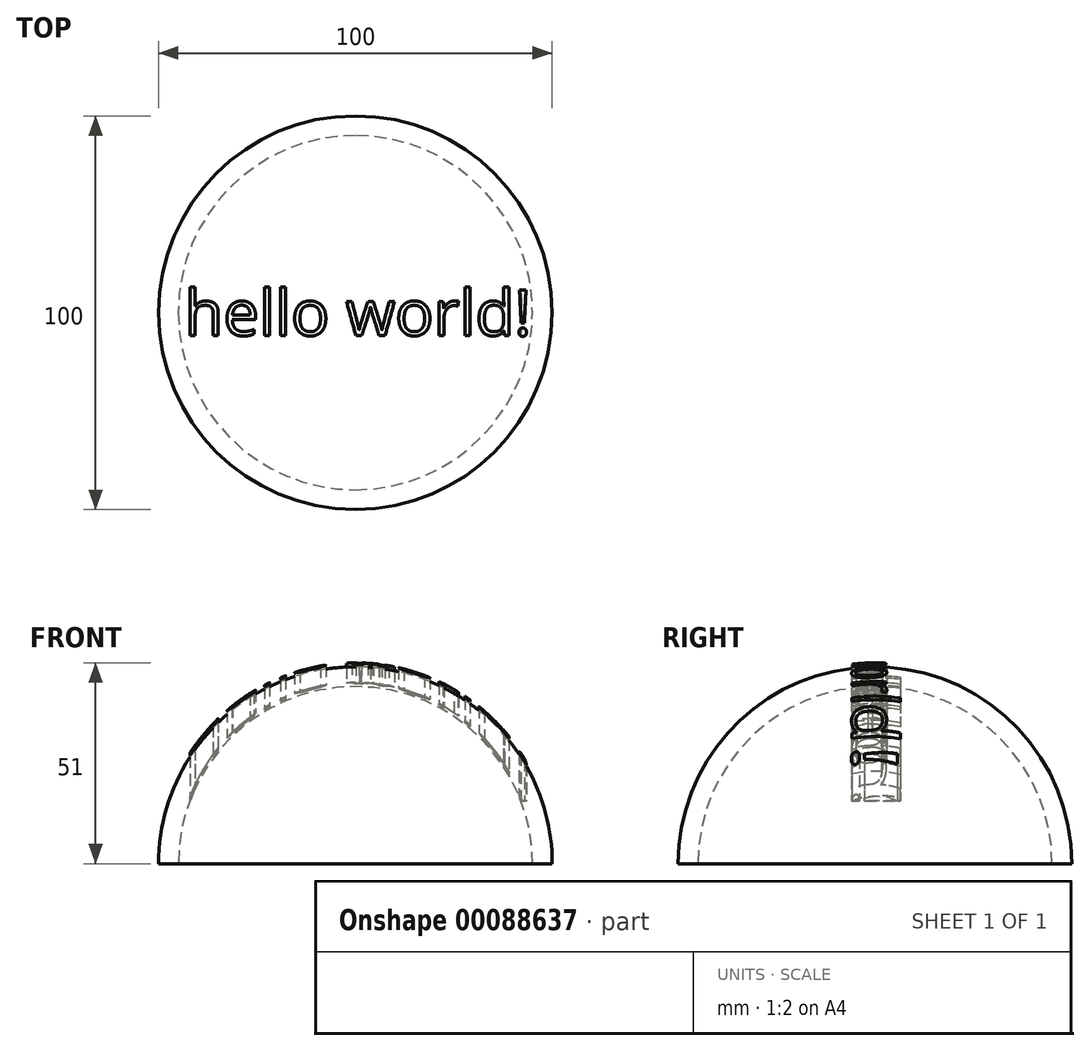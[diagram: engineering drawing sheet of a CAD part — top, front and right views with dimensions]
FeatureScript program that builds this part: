
annotation { "Feature Type Name" : "Feature", "Feature Type Description" : "" }
export const myFeature = defineFeature(function(context is Context, id is Id, definition is map)
    precondition{}
    {
        {
            var Q0;
            Q0=qCreatedBy(makeId("Top.planeOp"),FACE);
            var sketch = newSketch(context, id + "F0", { "sketchPlane" : qUnion([Q0])});
            skPoint(sketch, "E0", {"position": v(0, 50) * mm});
            skPoint(sketch, "E1", {"position": v(0, -50) * mm});
            skArc(sketch, "E2", {"start": v(0, 50) * mm, "mid": v(-50, 0) * mm, "end": v(0, -50) * mm});
            skPoint(sketch, "E3", {"position": v(0, 45) * mm});
            skPoint(sketch, "E4", {"position": v(0, -45) * mm});
            skArc(sketch, "E5", {"start": v(0, 45) * mm, "mid": v(-45, 0) * mm, "end": v(0, -45) * mm});
            skLineSegment(sketch, "E6", {"start": v(0, 45) * mm, "end": v(0, 50) * mm});
            skLineSegment(sketch, "E7", {"start": v(0, -45) * mm, "end": v(0, -50) * mm});
            skSolve(sketch);
        }
        {
            var Q0;
            Q0=makeQuery(id+"F0.imprint","IMPRINT",FACE,{"disambiguationData":[TD([[makeQuery(id+"F0.imprint","IMPRINT",EDGE,{"derivedFrom":sQuery(id+"F0.wireOp",EDGE,"E2")}),1.0]])]});
            var Q1;
            Q1=sQuery(id+"F0.wireOp",EDGE,"E6");
            revolve(context, id + "F1", {"entities" : qUnion([Q0]), "axis" : qUnion([Q1]), "revolveType" : RevolveType.ONE_DIRECTION, "angle" : 180 * degree});
        }
        {
            var Q0;
            Q0=makeQuery(id+"F1.opRevolve","SWEPT_BODY",BODY,{"disambiguationData":[OSD([sQuery(id+"F0.wireOp",EDGE,"E2"),sQuery(id+"F0.wireOp",EDGE,"E5"),sQuery(id+"F0.wireOp",EDGE,"E6"),sQuery(id+"F0.wireOp",EDGE,"E7")])]});
            transform(context, id + "F2", {"entities" : qUnion([Q0]), "transformType" : TransformType.TRANSLATION_3D, "dx" : 0 * mm, "dy" : 0 * mm, "dz" : 0 * mm, "makeCopy" : true});
        }
        {
            var Q0;
            Q0=qCreatedBy(makeId("Top.planeOp"),FACE);
            var sketch = newSketch(context, id + "F3", { "sketchPlane" : qUnion([Q0])});
            skText(sketch, "E8", { "text": "hello world!", "fontName": "OpenSans-Regular.ttf"});
            skLineSegment(sketch, "E9", {"start": v(-43.42, 5.8) * mm, "end": v(43.42, -5.8) * mm, "construction": true});
            skLineSegment(sketch, "E10", {"start": v(-43.42, -5.8) * mm, "end": v(43.42, 5.8) * mm, "construction": true});
            skPoint(sketch, "E11", {"position": v(0, 0) * mm});
            const initialGuessF3  = {"E8": [-0.04342, -0.0058, 1, 0, 0.0116]};
            skSetInitialGuess(sketch, initialGuessF3);
            skSolve(sketch);
        }
        {
            var Q0;
            Q0 = qSketchRegion(id + "F3", true);
            extrude(context, id + "F4", {"entities" : qUnion([Q0]), "endBound" : BoundingType.UP_TO_NEXT, "depth" : 100 * mm});
        }
        {
            var Q0;
            Q0=makeQuery(id+"F4.opExtrude","SWEPT_BODY",BODY,{"disambiguationData":[OSD([sQuery(id+"F3.wireOp",EDGE,"E8.sketch_text.stroke-0"),sQuery(id+"F3.wireOp",EDGE,"E8.sketch_text.stroke-1"),sQuery(id+"F3.wireOp",EDGE,"E8.sketch_text.stroke-2"),sQuery(id+"F3.wireOp",EDGE,"E8.sketch_text.stroke-3"),sQuery(id+"F3.wireOp",EDGE,"E8.sketch_text.stroke-4"),sQuery(id+"F3.wireOp",EDGE,"E8.sketch_text.stroke-5"),sQuery(id+"F3.wireOp",EDGE,"E8.sketch_text.stroke-6"),sQuery(id+"F3.wireOp",EDGE,"E8.sketch_text.stroke-7"),sQuery(id+"F3.wireOp",EDGE,"E8.sketch_text.stroke-8"),sQuery(id+"F3.wireOp",EDGE,"E8.sketch_text.stroke-9"),sQuery(id+"F3.wireOp",EDGE,"E8.sketch_text.stroke-10"),sQuery(id+"F3.wireOp",EDGE,"E8.sketch_text.stroke-11"),sQuery(id+"F3.wireOp",EDGE,"E8.sketch_text.stroke-12"),sQuery(id+"F3.wireOp",EDGE,"E8.sketch_text.stroke-13"),sQuery(id+"F3.wireOp",EDGE,"E8.sketch_text.stroke-14"),sQuery(id+"F3.wireOp",EDGE,"E8.sketch_text.stroke-15"),sQuery(id+"F3.wireOp",EDGE,"E8.sketch_text.stroke-16"),sQuery(id+"F3.wireOp",EDGE,"E8.sketch_text.stroke-17")])]});
            var Q1;
            Q1=makeQuery(id+"F4.opExtrude","SWEPT_BODY",BODY,{"disambiguationData":[OSD([sQuery(id+"F3.wireOp",EDGE,"E8.sketch_text.stroke-18"),sQuery(id+"F3.wireOp",EDGE,"E8.sketch_text.stroke-19"),sQuery(id+"F3.wireOp",EDGE,"E8.sketch_text.stroke-20"),sQuery(id+"F3.wireOp",EDGE,"E8.sketch_text.stroke-21"),sQuery(id+"F3.wireOp",EDGE,"E8.sketch_text.stroke-22"),sQuery(id+"F3.wireOp",EDGE,"E8.sketch_text.stroke-23"),sQuery(id+"F3.wireOp",EDGE,"E8.sketch_text.stroke-24"),sQuery(id+"F3.wireOp",EDGE,"E8.sketch_text.stroke-25"),sQuery(id+"F3.wireOp",EDGE,"E8.sketch_text.stroke-26"),sQuery(id+"F3.wireOp",EDGE,"E8.sketch_text.stroke-27"),sQuery(id+"F3.wireOp",EDGE,"E8.sketch_text.stroke-28"),sQuery(id+"F3.wireOp",EDGE,"E8.sketch_text.stroke-29"),sQuery(id+"F3.wireOp",EDGE,"E8.sketch_text.stroke-30"),sQuery(id+"F3.wireOp",EDGE,"E8.sketch_text.stroke-31"),sQuery(id+"F3.wireOp",EDGE,"E8.sketch_text.stroke-32"),sQuery(id+"F3.wireOp",EDGE,"E8.sketch_text.stroke-33"),sQuery(id+"F3.wireOp",EDGE,"E8.sketch_text.stroke-34"),sQuery(id+"F3.wireOp",EDGE,"E8.sketch_text.stroke-35"),sQuery(id+"F3.wireOp",EDGE,"E8.sketch_text.stroke-36")])]});
            var Q2;
            Q2=makeQuery(id+"F4.opExtrude","SWEPT_BODY",BODY,{"disambiguationData":[OSD([sQuery(id+"F3.wireOp",EDGE,"E8.sketch_text.stroke-37"),sQuery(id+"F3.wireOp",EDGE,"E8.sketch_text.stroke-38"),sQuery(id+"F3.wireOp",EDGE,"E8.sketch_text.stroke-39"),sQuery(id+"F3.wireOp",EDGE,"E8.sketch_text.stroke-40")])]});
            var Q3;
            Q3=makeQuery(id+"F4.opExtrude","SWEPT_BODY",BODY,{"disambiguationData":[OSD([sQuery(id+"F3.wireOp",EDGE,"E8.sketch_text.stroke-41"),sQuery(id+"F3.wireOp",EDGE,"E8.sketch_text.stroke-42"),sQuery(id+"F3.wireOp",EDGE,"E8.sketch_text.stroke-43"),sQuery(id+"F3.wireOp",EDGE,"E8.sketch_text.stroke-44")])]});
            var Q4;
            Q4=makeQuery(id+"F4.opExtrude","SWEPT_BODY",BODY,{"disambiguationData":[OSD([sQuery(id+"F3.wireOp",EDGE,"E8.sketch_text.stroke-45"),sQuery(id+"F3.wireOp",EDGE,"E8.sketch_text.stroke-46"),sQuery(id+"F3.wireOp",EDGE,"E8.sketch_text.stroke-47"),sQuery(id+"F3.wireOp",EDGE,"E8.sketch_text.stroke-48"),sQuery(id+"F3.wireOp",EDGE,"E8.sketch_text.stroke-49"),sQuery(id+"F3.wireOp",EDGE,"E8.sketch_text.stroke-50"),sQuery(id+"F3.wireOp",EDGE,"E8.sketch_text.stroke-51"),sQuery(id+"F3.wireOp",EDGE,"E8.sketch_text.stroke-52"),sQuery(id+"F3.wireOp",EDGE,"E8.sketch_text.stroke-53"),sQuery(id+"F3.wireOp",EDGE,"E8.sketch_text.stroke-54"),sQuery(id+"F3.wireOp",EDGE,"E8.sketch_text.stroke-55"),sQuery(id+"F3.wireOp",EDGE,"E8.sketch_text.stroke-56"),sQuery(id+"F3.wireOp",EDGE,"E8.sketch_text.stroke-57"),sQuery(id+"F3.wireOp",EDGE,"E8.sketch_text.stroke-58"),sQuery(id+"F3.wireOp",EDGE,"E8.sketch_text.stroke-59"),sQuery(id+"F3.wireOp",EDGE,"E8.sketch_text.stroke-60"),sQuery(id+"F3.wireOp",EDGE,"E8.sketch_text.stroke-61")])]});
            var Q5;
            Q5=makeQuery(id+"F4.opExtrude","SWEPT_BODY",BODY,{"disambiguationData":[OSD([sQuery(id+"F3.wireOp",EDGE,"E8.sketch_text.stroke-62"),sQuery(id+"F3.wireOp",EDGE,"E8.sketch_text.stroke-63"),sQuery(id+"F3.wireOp",EDGE,"E8.sketch_text.stroke-64"),sQuery(id+"F3.wireOp",EDGE,"E8.sketch_text.stroke-65"),sQuery(id+"F3.wireOp",EDGE,"E8.sketch_text.stroke-66"),sQuery(id+"F3.wireOp",EDGE,"E8.sketch_text.stroke-67"),sQuery(id+"F3.wireOp",EDGE,"E8.sketch_text.stroke-68"),sQuery(id+"F3.wireOp",EDGE,"E8.sketch_text.stroke-69"),sQuery(id+"F3.wireOp",EDGE,"E8.sketch_text.stroke-70"),sQuery(id+"F3.wireOp",EDGE,"E8.sketch_text.stroke-71"),sQuery(id+"F3.wireOp",EDGE,"E8.sketch_text.stroke-72"),sQuery(id+"F3.wireOp",EDGE,"E8.sketch_text.stroke-73"),sQuery(id+"F3.wireOp",EDGE,"E8.sketch_text.stroke-74"),sQuery(id+"F3.wireOp",EDGE,"E8.sketch_text.stroke-75"),sQuery(id+"F3.wireOp",EDGE,"E8.sketch_text.stroke-76"),sQuery(id+"F3.wireOp",EDGE,"E8.sketch_text.stroke-77"),sQuery(id+"F3.wireOp",EDGE,"E8.sketch_text.stroke-78"),sQuery(id+"F3.wireOp",EDGE,"E8.sketch_text.stroke-79"),sQuery(id+"F3.wireOp",EDGE,"E8.sketch_text.stroke-80"),sQuery(id+"F3.wireOp",EDGE,"E8.sketch_text.stroke-81"),sQuery(id+"F3.wireOp",EDGE,"E8.sketch_text.stroke-82"),sQuery(id+"F3.wireOp",EDGE,"E8.sketch_text.stroke-83"),sQuery(id+"F3.wireOp",EDGE,"E8.sketch_text.stroke-84")])]});
            var Q6;
            Q6=makeQuery(id+"F4.opExtrude","SWEPT_BODY",BODY,{"disambiguationData":[OSD([sQuery(id+"F3.wireOp",EDGE,"E8.sketch_text.stroke-85"),sQuery(id+"F3.wireOp",EDGE,"E8.sketch_text.stroke-86"),sQuery(id+"F3.wireOp",EDGE,"E8.sketch_text.stroke-87"),sQuery(id+"F3.wireOp",EDGE,"E8.sketch_text.stroke-88"),sQuery(id+"F3.wireOp",EDGE,"E8.sketch_text.stroke-89"),sQuery(id+"F3.wireOp",EDGE,"E8.sketch_text.stroke-90"),sQuery(id+"F3.wireOp",EDGE,"E8.sketch_text.stroke-91"),sQuery(id+"F3.wireOp",EDGE,"E8.sketch_text.stroke-92"),sQuery(id+"F3.wireOp",EDGE,"E8.sketch_text.stroke-93"),sQuery(id+"F3.wireOp",EDGE,"E8.sketch_text.stroke-94"),sQuery(id+"F3.wireOp",EDGE,"E8.sketch_text.stroke-95"),sQuery(id+"F3.wireOp",EDGE,"E8.sketch_text.stroke-96"),sQuery(id+"F3.wireOp",EDGE,"E8.sketch_text.stroke-97"),sQuery(id+"F3.wireOp",EDGE,"E8.sketch_text.stroke-98"),sQuery(id+"F3.wireOp",EDGE,"E8.sketch_text.stroke-99"),sQuery(id+"F3.wireOp",EDGE,"E8.sketch_text.stroke-100"),sQuery(id+"F3.wireOp",EDGE,"E8.sketch_text.stroke-101")])]});
            var Q7;
            Q7=makeQuery(id+"F4.opExtrude","SWEPT_BODY",BODY,{"disambiguationData":[OSD([sQuery(id+"F3.wireOp",EDGE,"E8.sketch_text.stroke-102"),sQuery(id+"F3.wireOp",EDGE,"E8.sketch_text.stroke-103"),sQuery(id+"F3.wireOp",EDGE,"E8.sketch_text.stroke-104"),sQuery(id+"F3.wireOp",EDGE,"E8.sketch_text.stroke-105"),sQuery(id+"F3.wireOp",EDGE,"E8.sketch_text.stroke-106"),sQuery(id+"F3.wireOp",EDGE,"E8.sketch_text.stroke-107"),sQuery(id+"F3.wireOp",EDGE,"E8.sketch_text.stroke-108"),sQuery(id+"F3.wireOp",EDGE,"E8.sketch_text.stroke-109"),sQuery(id+"F3.wireOp",EDGE,"E8.sketch_text.stroke-110"),sQuery(id+"F3.wireOp",EDGE,"E8.sketch_text.stroke-111"),sQuery(id+"F3.wireOp",EDGE,"E8.sketch_text.stroke-112"),sQuery(id+"F3.wireOp",EDGE,"E8.sketch_text.stroke-113"),sQuery(id+"F3.wireOp",EDGE,"E8.sketch_text.stroke-114")])]});
            var Q8;
            Q8=makeQuery(id+"F4.opExtrude","SWEPT_BODY",BODY,{"disambiguationData":[OSD([sQuery(id+"F3.wireOp",EDGE,"E8.sketch_text.stroke-115"),sQuery(id+"F3.wireOp",EDGE,"E8.sketch_text.stroke-116"),sQuery(id+"F3.wireOp",EDGE,"E8.sketch_text.stroke-117"),sQuery(id+"F3.wireOp",EDGE,"E8.sketch_text.stroke-118")])]});
            var Q9;
            Q9=makeQuery(id+"F4.opExtrude","SWEPT_BODY",BODY,{"disambiguationData":[OSD([sQuery(id+"F3.wireOp",EDGE,"E8.sketch_text.stroke-119"),sQuery(id+"F3.wireOp",EDGE,"E8.sketch_text.stroke-120"),sQuery(id+"F3.wireOp",EDGE,"E8.sketch_text.stroke-121"),sQuery(id+"F3.wireOp",EDGE,"E8.sketch_text.stroke-122"),sQuery(id+"F3.wireOp",EDGE,"E8.sketch_text.stroke-123"),sQuery(id+"F3.wireOp",EDGE,"E8.sketch_text.stroke-124"),sQuery(id+"F3.wireOp",EDGE,"E8.sketch_text.stroke-125"),sQuery(id+"F3.wireOp",EDGE,"E8.sketch_text.stroke-126"),sQuery(id+"F3.wireOp",EDGE,"E8.sketch_text.stroke-127"),sQuery(id+"F3.wireOp",EDGE,"E8.sketch_text.stroke-128"),sQuery(id+"F3.wireOp",EDGE,"E8.sketch_text.stroke-129"),sQuery(id+"F3.wireOp",EDGE,"E8.sketch_text.stroke-130"),sQuery(id+"F3.wireOp",EDGE,"E8.sketch_text.stroke-131"),sQuery(id+"F3.wireOp",EDGE,"E8.sketch_text.stroke-132"),sQuery(id+"F3.wireOp",EDGE,"E8.sketch_text.stroke-133"),sQuery(id+"F3.wireOp",EDGE,"E8.sketch_text.stroke-134"),sQuery(id+"F3.wireOp",EDGE,"E8.sketch_text.stroke-135"),sQuery(id+"F3.wireOp",EDGE,"E8.sketch_text.stroke-136"),sQuery(id+"F3.wireOp",EDGE,"E8.sketch_text.stroke-137"),sQuery(id+"F3.wireOp",EDGE,"E8.sketch_text.stroke-138"),sQuery(id+"F3.wireOp",EDGE,"E8.sketch_text.stroke-139"),sQuery(id+"F3.wireOp",EDGE,"E8.sketch_text.stroke-140"),sQuery(id+"F3.wireOp",EDGE,"E8.sketch_text.stroke-141"),sQuery(id+"F3.wireOp",EDGE,"E8.sketch_text.stroke-142")])]});
            var Q10;
            Q10=makeQuery(id+"F4.opExtrude","SWEPT_BODY",BODY,{"disambiguationData":[OSD([sQuery(id+"F3.wireOp",EDGE,"E8.sketch_text.stroke-143"),sQuery(id+"F3.wireOp",EDGE,"E8.sketch_text.stroke-144"),sQuery(id+"F3.wireOp",EDGE,"E8.sketch_text.stroke-145"),sQuery(id+"F3.wireOp",EDGE,"E8.sketch_text.stroke-146")])]});
            var Q11;
            Q11=makeQuery(id+"F4.opExtrude","SWEPT_BODY",BODY,{"disambiguationData":[OSD([sQuery(id+"F3.wireOp",EDGE,"E8.sketch_text.stroke-147"),sQuery(id+"F3.wireOp",EDGE,"E8.sketch_text.stroke-148"),sQuery(id+"F3.wireOp",EDGE,"E8.sketch_text.stroke-149"),sQuery(id+"F3.wireOp",EDGE,"E8.sketch_text.stroke-150"),sQuery(id+"F3.wireOp",EDGE,"E8.sketch_text.stroke-151"),sQuery(id+"F3.wireOp",EDGE,"E8.sketch_text.stroke-152"),sQuery(id+"F3.wireOp",EDGE,"E8.sketch_text.stroke-153")])]});
            transform(context, id + "F5", {"entities" : qUnion([Q0, Q1, Q2, Q3, Q4, Q5, Q6, Q7, Q8, Q9, Q10, Q11]), "transformType" : TransformType.TRANSLATION_3D, "dx" : 0 * mm, "dy" : 0 * mm, "dz" : 10 * mm, "makeCopy" : false});
        }
        {
            var Q0;
            Q0=makeQuery(id+"F4.opExtrude","SWEPT_BODY",BODY,{"disambiguationData":[OSD([sQuery(id+"F3.wireOp",EDGE,"E8.sketch_text.stroke-0"),sQuery(id+"F3.wireOp",EDGE,"E8.sketch_text.stroke-1"),sQuery(id+"F3.wireOp",EDGE,"E8.sketch_text.stroke-2"),sQuery(id+"F3.wireOp",EDGE,"E8.sketch_text.stroke-3"),sQuery(id+"F3.wireOp",EDGE,"E8.sketch_text.stroke-4"),sQuery(id+"F3.wireOp",EDGE,"E8.sketch_text.stroke-5"),sQuery(id+"F3.wireOp",EDGE,"E8.sketch_text.stroke-6"),sQuery(id+"F3.wireOp",EDGE,"E8.sketch_text.stroke-7"),sQuery(id+"F3.wireOp",EDGE,"E8.sketch_text.stroke-8"),sQuery(id+"F3.wireOp",EDGE,"E8.sketch_text.stroke-9"),sQuery(id+"F3.wireOp",EDGE,"E8.sketch_text.stroke-10"),sQuery(id+"F3.wireOp",EDGE,"E8.sketch_text.stroke-11"),sQuery(id+"F3.wireOp",EDGE,"E8.sketch_text.stroke-12"),sQuery(id+"F3.wireOp",EDGE,"E8.sketch_text.stroke-13"),sQuery(id+"F3.wireOp",EDGE,"E8.sketch_text.stroke-14"),sQuery(id+"F3.wireOp",EDGE,"E8.sketch_text.stroke-15"),sQuery(id+"F3.wireOp",EDGE,"E8.sketch_text.stroke-16"),sQuery(id+"F3.wireOp",EDGE,"E8.sketch_text.stroke-17")])]});
            var Q1;
            Q1=makeQuery(id+"F4.opExtrude","SWEPT_BODY",BODY,{"disambiguationData":[OSD([sQuery(id+"F3.wireOp",EDGE,"E8.sketch_text.stroke-18"),sQuery(id+"F3.wireOp",EDGE,"E8.sketch_text.stroke-19"),sQuery(id+"F3.wireOp",EDGE,"E8.sketch_text.stroke-20"),sQuery(id+"F3.wireOp",EDGE,"E8.sketch_text.stroke-21"),sQuery(id+"F3.wireOp",EDGE,"E8.sketch_text.stroke-22"),sQuery(id+"F3.wireOp",EDGE,"E8.sketch_text.stroke-23"),sQuery(id+"F3.wireOp",EDGE,"E8.sketch_text.stroke-24"),sQuery(id+"F3.wireOp",EDGE,"E8.sketch_text.stroke-25"),sQuery(id+"F3.wireOp",EDGE,"E8.sketch_text.stroke-26"),sQuery(id+"F3.wireOp",EDGE,"E8.sketch_text.stroke-27"),sQuery(id+"F3.wireOp",EDGE,"E8.sketch_text.stroke-28"),sQuery(id+"F3.wireOp",EDGE,"E8.sketch_text.stroke-29"),sQuery(id+"F3.wireOp",EDGE,"E8.sketch_text.stroke-30"),sQuery(id+"F3.wireOp",EDGE,"E8.sketch_text.stroke-31"),sQuery(id+"F3.wireOp",EDGE,"E8.sketch_text.stroke-32"),sQuery(id+"F3.wireOp",EDGE,"E8.sketch_text.stroke-33"),sQuery(id+"F3.wireOp",EDGE,"E8.sketch_text.stroke-34"),sQuery(id+"F3.wireOp",EDGE,"E8.sketch_text.stroke-35"),sQuery(id+"F3.wireOp",EDGE,"E8.sketch_text.stroke-36")])]});
            var Q2;
            Q2=makeQuery(id+"F4.opExtrude","SWEPT_BODY",BODY,{"disambiguationData":[OSD([sQuery(id+"F3.wireOp",EDGE,"E8.sketch_text.stroke-37"),sQuery(id+"F3.wireOp",EDGE,"E8.sketch_text.stroke-38"),sQuery(id+"F3.wireOp",EDGE,"E8.sketch_text.stroke-39"),sQuery(id+"F3.wireOp",EDGE,"E8.sketch_text.stroke-40")])]});
            var Q3;
            Q3=makeQuery(id+"F4.opExtrude","SWEPT_BODY",BODY,{"disambiguationData":[OSD([sQuery(id+"F3.wireOp",EDGE,"E8.sketch_text.stroke-41"),sQuery(id+"F3.wireOp",EDGE,"E8.sketch_text.stroke-42"),sQuery(id+"F3.wireOp",EDGE,"E8.sketch_text.stroke-43"),sQuery(id+"F3.wireOp",EDGE,"E8.sketch_text.stroke-44")])]});
            var Q4;
            Q4=makeQuery(id+"F4.opExtrude","SWEPT_BODY",BODY,{"disambiguationData":[OSD([sQuery(id+"F3.wireOp",EDGE,"E8.sketch_text.stroke-45"),sQuery(id+"F3.wireOp",EDGE,"E8.sketch_text.stroke-46"),sQuery(id+"F3.wireOp",EDGE,"E8.sketch_text.stroke-47"),sQuery(id+"F3.wireOp",EDGE,"E8.sketch_text.stroke-48"),sQuery(id+"F3.wireOp",EDGE,"E8.sketch_text.stroke-49"),sQuery(id+"F3.wireOp",EDGE,"E8.sketch_text.stroke-50"),sQuery(id+"F3.wireOp",EDGE,"E8.sketch_text.stroke-51"),sQuery(id+"F3.wireOp",EDGE,"E8.sketch_text.stroke-52"),sQuery(id+"F3.wireOp",EDGE,"E8.sketch_text.stroke-53"),sQuery(id+"F3.wireOp",EDGE,"E8.sketch_text.stroke-54"),sQuery(id+"F3.wireOp",EDGE,"E8.sketch_text.stroke-55"),sQuery(id+"F3.wireOp",EDGE,"E8.sketch_text.stroke-56"),sQuery(id+"F3.wireOp",EDGE,"E8.sketch_text.stroke-57"),sQuery(id+"F3.wireOp",EDGE,"E8.sketch_text.stroke-58"),sQuery(id+"F3.wireOp",EDGE,"E8.sketch_text.stroke-59"),sQuery(id+"F3.wireOp",EDGE,"E8.sketch_text.stroke-60"),sQuery(id+"F3.wireOp",EDGE,"E8.sketch_text.stroke-61")])]});
            var Q5;
            Q5=makeQuery(id+"F4.opExtrude","SWEPT_BODY",BODY,{"disambiguationData":[OSD([sQuery(id+"F3.wireOp",EDGE,"E8.sketch_text.stroke-62"),sQuery(id+"F3.wireOp",EDGE,"E8.sketch_text.stroke-63"),sQuery(id+"F3.wireOp",EDGE,"E8.sketch_text.stroke-64"),sQuery(id+"F3.wireOp",EDGE,"E8.sketch_text.stroke-65"),sQuery(id+"F3.wireOp",EDGE,"E8.sketch_text.stroke-66"),sQuery(id+"F3.wireOp",EDGE,"E8.sketch_text.stroke-67"),sQuery(id+"F3.wireOp",EDGE,"E8.sketch_text.stroke-68"),sQuery(id+"F3.wireOp",EDGE,"E8.sketch_text.stroke-69"),sQuery(id+"F3.wireOp",EDGE,"E8.sketch_text.stroke-70"),sQuery(id+"F3.wireOp",EDGE,"E8.sketch_text.stroke-71"),sQuery(id+"F3.wireOp",EDGE,"E8.sketch_text.stroke-72"),sQuery(id+"F3.wireOp",EDGE,"E8.sketch_text.stroke-73"),sQuery(id+"F3.wireOp",EDGE,"E8.sketch_text.stroke-74"),sQuery(id+"F3.wireOp",EDGE,"E8.sketch_text.stroke-75"),sQuery(id+"F3.wireOp",EDGE,"E8.sketch_text.stroke-76"),sQuery(id+"F3.wireOp",EDGE,"E8.sketch_text.stroke-77"),sQuery(id+"F3.wireOp",EDGE,"E8.sketch_text.stroke-78"),sQuery(id+"F3.wireOp",EDGE,"E8.sketch_text.stroke-79"),sQuery(id+"F3.wireOp",EDGE,"E8.sketch_text.stroke-80"),sQuery(id+"F3.wireOp",EDGE,"E8.sketch_text.stroke-81"),sQuery(id+"F3.wireOp",EDGE,"E8.sketch_text.stroke-82"),sQuery(id+"F3.wireOp",EDGE,"E8.sketch_text.stroke-83"),sQuery(id+"F3.wireOp",EDGE,"E8.sketch_text.stroke-84")])]});
            var Q6;
            Q6=makeQuery(id+"F4.opExtrude","SWEPT_BODY",BODY,{"disambiguationData":[OSD([sQuery(id+"F3.wireOp",EDGE,"E8.sketch_text.stroke-85"),sQuery(id+"F3.wireOp",EDGE,"E8.sketch_text.stroke-86"),sQuery(id+"F3.wireOp",EDGE,"E8.sketch_text.stroke-87"),sQuery(id+"F3.wireOp",EDGE,"E8.sketch_text.stroke-88"),sQuery(id+"F3.wireOp",EDGE,"E8.sketch_text.stroke-89"),sQuery(id+"F3.wireOp",EDGE,"E8.sketch_text.stroke-90"),sQuery(id+"F3.wireOp",EDGE,"E8.sketch_text.stroke-91"),sQuery(id+"F3.wireOp",EDGE,"E8.sketch_text.stroke-92"),sQuery(id+"F3.wireOp",EDGE,"E8.sketch_text.stroke-93"),sQuery(id+"F3.wireOp",EDGE,"E8.sketch_text.stroke-94"),sQuery(id+"F3.wireOp",EDGE,"E8.sketch_text.stroke-95"),sQuery(id+"F3.wireOp",EDGE,"E8.sketch_text.stroke-96"),sQuery(id+"F3.wireOp",EDGE,"E8.sketch_text.stroke-97"),sQuery(id+"F3.wireOp",EDGE,"E8.sketch_text.stroke-98"),sQuery(id+"F3.wireOp",EDGE,"E8.sketch_text.stroke-99"),sQuery(id+"F3.wireOp",EDGE,"E8.sketch_text.stroke-100"),sQuery(id+"F3.wireOp",EDGE,"E8.sketch_text.stroke-101")])]});
            var Q7;
            Q7=makeQuery(id+"F4.opExtrude","SWEPT_BODY",BODY,{"disambiguationData":[OSD([sQuery(id+"F3.wireOp",EDGE,"E8.sketch_text.stroke-102"),sQuery(id+"F3.wireOp",EDGE,"E8.sketch_text.stroke-103"),sQuery(id+"F3.wireOp",EDGE,"E8.sketch_text.stroke-104"),sQuery(id+"F3.wireOp",EDGE,"E8.sketch_text.stroke-105"),sQuery(id+"F3.wireOp",EDGE,"E8.sketch_text.stroke-106"),sQuery(id+"F3.wireOp",EDGE,"E8.sketch_text.stroke-107"),sQuery(id+"F3.wireOp",EDGE,"E8.sketch_text.stroke-108"),sQuery(id+"F3.wireOp",EDGE,"E8.sketch_text.stroke-109"),sQuery(id+"F3.wireOp",EDGE,"E8.sketch_text.stroke-110"),sQuery(id+"F3.wireOp",EDGE,"E8.sketch_text.stroke-111"),sQuery(id+"F3.wireOp",EDGE,"E8.sketch_text.stroke-112"),sQuery(id+"F3.wireOp",EDGE,"E8.sketch_text.stroke-113"),sQuery(id+"F3.wireOp",EDGE,"E8.sketch_text.stroke-114")])]});
            var Q8;
            Q8=makeQuery(id+"F4.opExtrude","SWEPT_BODY",BODY,{"disambiguationData":[OSD([sQuery(id+"F3.wireOp",EDGE,"E8.sketch_text.stroke-115"),sQuery(id+"F3.wireOp",EDGE,"E8.sketch_text.stroke-116"),sQuery(id+"F3.wireOp",EDGE,"E8.sketch_text.stroke-117"),sQuery(id+"F3.wireOp",EDGE,"E8.sketch_text.stroke-118")])]});
            var Q9;
            Q9=makeQuery(id+"F4.opExtrude","SWEPT_BODY",BODY,{"disambiguationData":[OSD([sQuery(id+"F3.wireOp",EDGE,"E8.sketch_text.stroke-119"),sQuery(id+"F3.wireOp",EDGE,"E8.sketch_text.stroke-120"),sQuery(id+"F3.wireOp",EDGE,"E8.sketch_text.stroke-121"),sQuery(id+"F3.wireOp",EDGE,"E8.sketch_text.stroke-122"),sQuery(id+"F3.wireOp",EDGE,"E8.sketch_text.stroke-123"),sQuery(id+"F3.wireOp",EDGE,"E8.sketch_text.stroke-124"),sQuery(id+"F3.wireOp",EDGE,"E8.sketch_text.stroke-125"),sQuery(id+"F3.wireOp",EDGE,"E8.sketch_text.stroke-126"),sQuery(id+"F3.wireOp",EDGE,"E8.sketch_text.stroke-127"),sQuery(id+"F3.wireOp",EDGE,"E8.sketch_text.stroke-128"),sQuery(id+"F3.wireOp",EDGE,"E8.sketch_text.stroke-129"),sQuery(id+"F3.wireOp",EDGE,"E8.sketch_text.stroke-130"),sQuery(id+"F3.wireOp",EDGE,"E8.sketch_text.stroke-131"),sQuery(id+"F3.wireOp",EDGE,"E8.sketch_text.stroke-132"),sQuery(id+"F3.wireOp",EDGE,"E8.sketch_text.stroke-133"),sQuery(id+"F3.wireOp",EDGE,"E8.sketch_text.stroke-134"),sQuery(id+"F3.wireOp",EDGE,"E8.sketch_text.stroke-135"),sQuery(id+"F3.wireOp",EDGE,"E8.sketch_text.stroke-136"),sQuery(id+"F3.wireOp",EDGE,"E8.sketch_text.stroke-137"),sQuery(id+"F3.wireOp",EDGE,"E8.sketch_text.stroke-138"),sQuery(id+"F3.wireOp",EDGE,"E8.sketch_text.stroke-139"),sQuery(id+"F3.wireOp",EDGE,"E8.sketch_text.stroke-140"),sQuery(id+"F3.wireOp",EDGE,"E8.sketch_text.stroke-141"),sQuery(id+"F3.wireOp",EDGE,"E8.sketch_text.stroke-142")])]});
            var Q10;
            Q10=makeQuery(id+"F4.opExtrude","SWEPT_BODY",BODY,{"disambiguationData":[OSD([sQuery(id+"F3.wireOp",EDGE,"E8.sketch_text.stroke-143"),sQuery(id+"F3.wireOp",EDGE,"E8.sketch_text.stroke-144"),sQuery(id+"F3.wireOp",EDGE,"E8.sketch_text.stroke-145"),sQuery(id+"F3.wireOp",EDGE,"E8.sketch_text.stroke-146")])]});
            var Q11;
            Q11=makeQuery(id+"F4.opExtrude","SWEPT_BODY",BODY,{"disambiguationData":[OSD([sQuery(id+"F3.wireOp",EDGE,"E8.sketch_text.stroke-147"),sQuery(id+"F3.wireOp",EDGE,"E8.sketch_text.stroke-148"),sQuery(id+"F3.wireOp",EDGE,"E8.sketch_text.stroke-149"),sQuery(id+"F3.wireOp",EDGE,"E8.sketch_text.stroke-150"),sQuery(id+"F3.wireOp",EDGE,"E8.sketch_text.stroke-151"),sQuery(id+"F3.wireOp",EDGE,"E8.sketch_text.stroke-152"),sQuery(id+"F3.wireOp",EDGE,"E8.sketch_text.stroke-153")])]});
            var Q12;
            Q12=makeQuery(id+"F2.opPattern","COPY",BODY,{"derivedFrom":makeQuery(id+"F1.opRevolve","SWEPT_BODY",BODY,{"disambiguationData":[OSD([sQuery(id+"F0.wireOp",EDGE,"E2"),sQuery(id+"F0.wireOp",EDGE,"E5"),sQuery(id+"F0.wireOp",EDGE,"E6"),sQuery(id+"F0.wireOp",EDGE,"E7")])]}),"instanceName":"1"});
            transform(context, id + "F6", {"entities" : qUnion([Q0, Q1, Q2, Q3, Q4, Q5, Q6, Q7, Q8, Q9, Q10, Q11, Q12]), "transformType" : TransformType.TRANSLATION_3D, "dx" : 0 * mm, "dy" : 0 * mm, "dz" : 5 * mm, "makeCopy" : false});
        }
        {
            var Q0;
            Q0=makeQuery(id+"F2.opPattern","COPY",BODY,{"derivedFrom":makeQuery(id+"F1.opRevolve","SWEPT_BODY",BODY,{"disambiguationData":[OSD([sQuery(id+"F0.wireOp",EDGE,"E2"),sQuery(id+"F0.wireOp",EDGE,"E5"),sQuery(id+"F0.wireOp",EDGE,"E6"),sQuery(id+"F0.wireOp",EDGE,"E7")])]}),"instanceName":"1"});
            deleteBodies(context, id + "F7", {"entities" : qUnion([Q0])});
        }
        {
            var Q0;
            Q0=makeQuery(id+"F1.opRevolve","SWEPT_BODY",BODY,{"disambiguationData":[OSD([sQuery(id+"F0.wireOp",EDGE,"E2"),sQuery(id+"F0.wireOp",EDGE,"E5"),sQuery(id+"F0.wireOp",EDGE,"E6"),sQuery(id+"F0.wireOp",EDGE,"E7")])]});
            transform(context, id + "F8", {"entities" : qUnion([Q0]), "transformType" : TransformType.TRANSLATION_3D, "dx" : 0 * mm, "dy" : 0 * mm, "dz" : 0 * mm, "makeCopy" : true});
        }
        {
            var Q0;
            Q0=makeQuery(id+"F8.opPattern","COPY",BODY,{"derivedFrom":makeQuery(id+"F1.opRevolve","SWEPT_BODY",BODY,{"disambiguationData":[OSD([sQuery(id+"F0.wireOp",EDGE,"E2"),sQuery(id+"F0.wireOp",EDGE,"E5"),sQuery(id+"F0.wireOp",EDGE,"E6"),sQuery(id+"F0.wireOp",EDGE,"E7")])]}),"instanceName":"1"});
            var Q1;
            Q1=makeQuery(id+"F4.opExtrude","SWEPT_BODY",BODY,{"disambiguationData":[OSD([sQuery(id+"F3.wireOp",EDGE,"E8.sketch_text.stroke-0"),sQuery(id+"F3.wireOp",EDGE,"E8.sketch_text.stroke-1"),sQuery(id+"F3.wireOp",EDGE,"E8.sketch_text.stroke-2"),sQuery(id+"F3.wireOp",EDGE,"E8.sketch_text.stroke-3"),sQuery(id+"F3.wireOp",EDGE,"E8.sketch_text.stroke-4"),sQuery(id+"F3.wireOp",EDGE,"E8.sketch_text.stroke-5"),sQuery(id+"F3.wireOp",EDGE,"E8.sketch_text.stroke-6"),sQuery(id+"F3.wireOp",EDGE,"E8.sketch_text.stroke-7"),sQuery(id+"F3.wireOp",EDGE,"E8.sketch_text.stroke-8"),sQuery(id+"F3.wireOp",EDGE,"E8.sketch_text.stroke-9"),sQuery(id+"F3.wireOp",EDGE,"E8.sketch_text.stroke-10"),sQuery(id+"F3.wireOp",EDGE,"E8.sketch_text.stroke-11"),sQuery(id+"F3.wireOp",EDGE,"E8.sketch_text.stroke-12"),sQuery(id+"F3.wireOp",EDGE,"E8.sketch_text.stroke-13"),sQuery(id+"F3.wireOp",EDGE,"E8.sketch_text.stroke-14"),sQuery(id+"F3.wireOp",EDGE,"E8.sketch_text.stroke-15"),sQuery(id+"F3.wireOp",EDGE,"E8.sketch_text.stroke-16"),sQuery(id+"F3.wireOp",EDGE,"E8.sketch_text.stroke-17")])]});
            booleanBodies(context, id + "F9", {"operationType" : BooleanOperationType.INTERSECTION, "tools" : qUnion([Q0, Q1]), "keepTools" : true});
        }
        {
            var Q0;
            Q0=makeQuery(id+"F8.opPattern","COPY",BODY,{"derivedFrom":makeQuery(id+"F1.opRevolve","SWEPT_BODY",BODY,{"disambiguationData":[OSD([sQuery(id+"F0.wireOp",EDGE,"E2"),sQuery(id+"F0.wireOp",EDGE,"E5"),sQuery(id+"F0.wireOp",EDGE,"E6"),sQuery(id+"F0.wireOp",EDGE,"E7")])]}),"instanceName":"1"});
            var Q1;
            Q1=makeQuery(id+"F4.opExtrude","SWEPT_BODY",BODY,{"disambiguationData":[OSD([sQuery(id+"F3.wireOp",EDGE,"E8.sketch_text.stroke-18"),sQuery(id+"F3.wireOp",EDGE,"E8.sketch_text.stroke-19"),sQuery(id+"F3.wireOp",EDGE,"E8.sketch_text.stroke-20"),sQuery(id+"F3.wireOp",EDGE,"E8.sketch_text.stroke-21"),sQuery(id+"F3.wireOp",EDGE,"E8.sketch_text.stroke-22"),sQuery(id+"F3.wireOp",EDGE,"E8.sketch_text.stroke-23"),sQuery(id+"F3.wireOp",EDGE,"E8.sketch_text.stroke-24"),sQuery(id+"F3.wireOp",EDGE,"E8.sketch_text.stroke-25"),sQuery(id+"F3.wireOp",EDGE,"E8.sketch_text.stroke-26"),sQuery(id+"F3.wireOp",EDGE,"E8.sketch_text.stroke-27"),sQuery(id+"F3.wireOp",EDGE,"E8.sketch_text.stroke-28"),sQuery(id+"F3.wireOp",EDGE,"E8.sketch_text.stroke-29"),sQuery(id+"F3.wireOp",EDGE,"E8.sketch_text.stroke-30"),sQuery(id+"F3.wireOp",EDGE,"E8.sketch_text.stroke-31"),sQuery(id+"F3.wireOp",EDGE,"E8.sketch_text.stroke-32"),sQuery(id+"F3.wireOp",EDGE,"E8.sketch_text.stroke-33"),sQuery(id+"F3.wireOp",EDGE,"E8.sketch_text.stroke-34"),sQuery(id+"F3.wireOp",EDGE,"E8.sketch_text.stroke-35"),sQuery(id+"F3.wireOp",EDGE,"E8.sketch_text.stroke-36")])]});
            booleanBodies(context, id + "F10", {"operationType" : BooleanOperationType.INTERSECTION, "tools" : qUnion([Q0, Q1]), "keepTools" : true});
        }
        {
            var Q0;
            Q0=makeQuery(id+"F8.opPattern","COPY",BODY,{"derivedFrom":makeQuery(id+"F1.opRevolve","SWEPT_BODY",BODY,{"disambiguationData":[OSD([sQuery(id+"F0.wireOp",EDGE,"E2"),sQuery(id+"F0.wireOp",EDGE,"E5"),sQuery(id+"F0.wireOp",EDGE,"E6"),sQuery(id+"F0.wireOp",EDGE,"E7")])]}),"instanceName":"1"});
            var Q1;
            Q1=makeQuery(id+"F4.opExtrude","SWEPT_BODY",BODY,{"disambiguationData":[OSD([sQuery(id+"F3.wireOp",EDGE,"E8.sketch_text.stroke-37"),sQuery(id+"F3.wireOp",EDGE,"E8.sketch_text.stroke-38"),sQuery(id+"F3.wireOp",EDGE,"E8.sketch_text.stroke-39"),sQuery(id+"F3.wireOp",EDGE,"E8.sketch_text.stroke-40")])]});
            booleanBodies(context, id + "F11", {"operationType" : BooleanOperationType.INTERSECTION, "tools" : qUnion([Q0, Q1]), "keepTools" : true});
        }
        {
            var Q0;
            Q0=makeQuery(id+"F4.opExtrude","SWEPT_BODY",BODY,{"disambiguationData":[OSD([sQuery(id+"F3.wireOp",EDGE,"E8.sketch_text.stroke-41"),sQuery(id+"F3.wireOp",EDGE,"E8.sketch_text.stroke-42"),sQuery(id+"F3.wireOp",EDGE,"E8.sketch_text.stroke-43"),sQuery(id+"F3.wireOp",EDGE,"E8.sketch_text.stroke-44")])]});
            var Q1;
            Q1=makeQuery(id+"F8.opPattern","COPY",BODY,{"derivedFrom":makeQuery(id+"F1.opRevolve","SWEPT_BODY",BODY,{"disambiguationData":[OSD([sQuery(id+"F0.wireOp",EDGE,"E2"),sQuery(id+"F0.wireOp",EDGE,"E5"),sQuery(id+"F0.wireOp",EDGE,"E6"),sQuery(id+"F0.wireOp",EDGE,"E7")])]}),"instanceName":"1"});
            booleanBodies(context, id + "F12", {"operationType" : BooleanOperationType.INTERSECTION, "tools" : qUnion([Q0, Q1]), "keepTools" : true});
        }
        {
            var Q0;
            Q0=makeQuery(id+"F8.opPattern","COPY",BODY,{"derivedFrom":makeQuery(id+"F1.opRevolve","SWEPT_BODY",BODY,{"disambiguationData":[OSD([sQuery(id+"F0.wireOp",EDGE,"E2"),sQuery(id+"F0.wireOp",EDGE,"E5"),sQuery(id+"F0.wireOp",EDGE,"E6"),sQuery(id+"F0.wireOp",EDGE,"E7")])]}),"instanceName":"1"});
            var Q1;
            Q1=makeQuery(id+"F4.opExtrude","SWEPT_BODY",BODY,{"disambiguationData":[OSD([sQuery(id+"F3.wireOp",EDGE,"E8.sketch_text.stroke-45"),sQuery(id+"F3.wireOp",EDGE,"E8.sketch_text.stroke-46"),sQuery(id+"F3.wireOp",EDGE,"E8.sketch_text.stroke-47"),sQuery(id+"F3.wireOp",EDGE,"E8.sketch_text.stroke-48"),sQuery(id+"F3.wireOp",EDGE,"E8.sketch_text.stroke-49"),sQuery(id+"F3.wireOp",EDGE,"E8.sketch_text.stroke-50"),sQuery(id+"F3.wireOp",EDGE,"E8.sketch_text.stroke-51"),sQuery(id+"F3.wireOp",EDGE,"E8.sketch_text.stroke-52"),sQuery(id+"F3.wireOp",EDGE,"E8.sketch_text.stroke-53"),sQuery(id+"F3.wireOp",EDGE,"E8.sketch_text.stroke-54"),sQuery(id+"F3.wireOp",EDGE,"E8.sketch_text.stroke-55"),sQuery(id+"F3.wireOp",EDGE,"E8.sketch_text.stroke-56"),sQuery(id+"F3.wireOp",EDGE,"E8.sketch_text.stroke-57"),sQuery(id+"F3.wireOp",EDGE,"E8.sketch_text.stroke-58"),sQuery(id+"F3.wireOp",EDGE,"E8.sketch_text.stroke-59"),sQuery(id+"F3.wireOp",EDGE,"E8.sketch_text.stroke-60"),sQuery(id+"F3.wireOp",EDGE,"E8.sketch_text.stroke-61")])]});
            booleanBodies(context, id + "F13", {"operationType" : BooleanOperationType.INTERSECTION, "tools" : qUnion([Q0, Q1]), "keepTools" : true});
        }
        {
            var Q0;
            Q0=makeQuery(id+"F8.opPattern","COPY",BODY,{"derivedFrom":makeQuery(id+"F1.opRevolve","SWEPT_BODY",BODY,{"disambiguationData":[OSD([sQuery(id+"F0.wireOp",EDGE,"E2"),sQuery(id+"F0.wireOp",EDGE,"E5"),sQuery(id+"F0.wireOp",EDGE,"E6"),sQuery(id+"F0.wireOp",EDGE,"E7")])]}),"instanceName":"1"});
            var Q1;
            Q1=makeQuery(id+"F4.opExtrude","SWEPT_BODY",BODY,{"disambiguationData":[OSD([sQuery(id+"F3.wireOp",EDGE,"E8.sketch_text.stroke-62"),sQuery(id+"F3.wireOp",EDGE,"E8.sketch_text.stroke-63"),sQuery(id+"F3.wireOp",EDGE,"E8.sketch_text.stroke-64"),sQuery(id+"F3.wireOp",EDGE,"E8.sketch_text.stroke-65"),sQuery(id+"F3.wireOp",EDGE,"E8.sketch_text.stroke-66"),sQuery(id+"F3.wireOp",EDGE,"E8.sketch_text.stroke-67"),sQuery(id+"F3.wireOp",EDGE,"E8.sketch_text.stroke-68"),sQuery(id+"F3.wireOp",EDGE,"E8.sketch_text.stroke-69"),sQuery(id+"F3.wireOp",EDGE,"E8.sketch_text.stroke-70"),sQuery(id+"F3.wireOp",EDGE,"E8.sketch_text.stroke-71"),sQuery(id+"F3.wireOp",EDGE,"E8.sketch_text.stroke-72"),sQuery(id+"F3.wireOp",EDGE,"E8.sketch_text.stroke-73"),sQuery(id+"F3.wireOp",EDGE,"E8.sketch_text.stroke-74"),sQuery(id+"F3.wireOp",EDGE,"E8.sketch_text.stroke-75"),sQuery(id+"F3.wireOp",EDGE,"E8.sketch_text.stroke-76"),sQuery(id+"F3.wireOp",EDGE,"E8.sketch_text.stroke-77"),sQuery(id+"F3.wireOp",EDGE,"E8.sketch_text.stroke-78"),sQuery(id+"F3.wireOp",EDGE,"E8.sketch_text.stroke-79"),sQuery(id+"F3.wireOp",EDGE,"E8.sketch_text.stroke-80"),sQuery(id+"F3.wireOp",EDGE,"E8.sketch_text.stroke-81"),sQuery(id+"F3.wireOp",EDGE,"E8.sketch_text.stroke-82"),sQuery(id+"F3.wireOp",EDGE,"E8.sketch_text.stroke-83"),sQuery(id+"F3.wireOp",EDGE,"E8.sketch_text.stroke-84")])]});
            booleanBodies(context, id + "F14", {"operationType" : BooleanOperationType.INTERSECTION, "tools" : qUnion([Q0, Q1]), "keepTools" : true});
        }
        {
            var Q0;
            Q0=makeQuery(id+"F4.opExtrude","SWEPT_BODY",BODY,{"disambiguationData":[OSD([sQuery(id+"F3.wireOp",EDGE,"E8.sketch_text.stroke-85"),sQuery(id+"F3.wireOp",EDGE,"E8.sketch_text.stroke-86"),sQuery(id+"F3.wireOp",EDGE,"E8.sketch_text.stroke-87"),sQuery(id+"F3.wireOp",EDGE,"E8.sketch_text.stroke-88"),sQuery(id+"F3.wireOp",EDGE,"E8.sketch_text.stroke-89"),sQuery(id+"F3.wireOp",EDGE,"E8.sketch_text.stroke-90"),sQuery(id+"F3.wireOp",EDGE,"E8.sketch_text.stroke-91"),sQuery(id+"F3.wireOp",EDGE,"E8.sketch_text.stroke-92"),sQuery(id+"F3.wireOp",EDGE,"E8.sketch_text.stroke-93"),sQuery(id+"F3.wireOp",EDGE,"E8.sketch_text.stroke-94"),sQuery(id+"F3.wireOp",EDGE,"E8.sketch_text.stroke-95"),sQuery(id+"F3.wireOp",EDGE,"E8.sketch_text.stroke-96"),sQuery(id+"F3.wireOp",EDGE,"E8.sketch_text.stroke-97"),sQuery(id+"F3.wireOp",EDGE,"E8.sketch_text.stroke-98"),sQuery(id+"F3.wireOp",EDGE,"E8.sketch_text.stroke-99"),sQuery(id+"F3.wireOp",EDGE,"E8.sketch_text.stroke-100"),sQuery(id+"F3.wireOp",EDGE,"E8.sketch_text.stroke-101")])]});
            var Q1;
            Q1=makeQuery(id+"F8.opPattern","COPY",BODY,{"derivedFrom":makeQuery(id+"F1.opRevolve","SWEPT_BODY",BODY,{"disambiguationData":[OSD([sQuery(id+"F0.wireOp",EDGE,"E2"),sQuery(id+"F0.wireOp",EDGE,"E5"),sQuery(id+"F0.wireOp",EDGE,"E6"),sQuery(id+"F0.wireOp",EDGE,"E7")])]}),"instanceName":"1"});
            booleanBodies(context, id + "F15", {"operationType" : BooleanOperationType.INTERSECTION, "tools" : qUnion([Q0, Q1]), "keepTools" : true});
        }
        {
            var Q0;
            Q0=makeQuery(id+"F4.opExtrude","SWEPT_BODY",BODY,{"disambiguationData":[OSD([sQuery(id+"F3.wireOp",EDGE,"E8.sketch_text.stroke-102"),sQuery(id+"F3.wireOp",EDGE,"E8.sketch_text.stroke-103"),sQuery(id+"F3.wireOp",EDGE,"E8.sketch_text.stroke-104"),sQuery(id+"F3.wireOp",EDGE,"E8.sketch_text.stroke-105"),sQuery(id+"F3.wireOp",EDGE,"E8.sketch_text.stroke-106"),sQuery(id+"F3.wireOp",EDGE,"E8.sketch_text.stroke-107"),sQuery(id+"F3.wireOp",EDGE,"E8.sketch_text.stroke-108"),sQuery(id+"F3.wireOp",EDGE,"E8.sketch_text.stroke-109"),sQuery(id+"F3.wireOp",EDGE,"E8.sketch_text.stroke-110"),sQuery(id+"F3.wireOp",EDGE,"E8.sketch_text.stroke-111"),sQuery(id+"F3.wireOp",EDGE,"E8.sketch_text.stroke-112"),sQuery(id+"F3.wireOp",EDGE,"E8.sketch_text.stroke-113"),sQuery(id+"F3.wireOp",EDGE,"E8.sketch_text.stroke-114")])]});
            var Q1;
            Q1=makeQuery(id+"F8.opPattern","COPY",BODY,{"derivedFrom":makeQuery(id+"F1.opRevolve","SWEPT_BODY",BODY,{"disambiguationData":[OSD([sQuery(id+"F0.wireOp",EDGE,"E2"),sQuery(id+"F0.wireOp",EDGE,"E5"),sQuery(id+"F0.wireOp",EDGE,"E6"),sQuery(id+"F0.wireOp",EDGE,"E7")])]}),"instanceName":"1"});
            booleanBodies(context, id + "F16", {"operationType" : BooleanOperationType.INTERSECTION, "tools" : qUnion([Q0, Q1]), "keepTools" : true});
        }
        {
            var Q0;
            Q0=makeQuery(id+"F4.opExtrude","SWEPT_BODY",BODY,{"disambiguationData":[OSD([sQuery(id+"F3.wireOp",EDGE,"E8.sketch_text.stroke-115"),sQuery(id+"F3.wireOp",EDGE,"E8.sketch_text.stroke-116"),sQuery(id+"F3.wireOp",EDGE,"E8.sketch_text.stroke-117"),sQuery(id+"F3.wireOp",EDGE,"E8.sketch_text.stroke-118")])]});
            var Q1;
            Q1=makeQuery(id+"F8.opPattern","COPY",BODY,{"derivedFrom":makeQuery(id+"F1.opRevolve","SWEPT_BODY",BODY,{"disambiguationData":[OSD([sQuery(id+"F0.wireOp",EDGE,"E2"),sQuery(id+"F0.wireOp",EDGE,"E5"),sQuery(id+"F0.wireOp",EDGE,"E6"),sQuery(id+"F0.wireOp",EDGE,"E7")])]}),"instanceName":"1"});
            booleanBodies(context, id + "F17", {"operationType" : BooleanOperationType.INTERSECTION, "tools" : qUnion([Q0, Q1]), "keepTools" : true});
        }
        {
            var Q0;
            Q0=makeQuery(id+"F4.opExtrude","SWEPT_BODY",BODY,{"disambiguationData":[OSD([sQuery(id+"F3.wireOp",EDGE,"E8.sketch_text.stroke-115"),sQuery(id+"F3.wireOp",EDGE,"E8.sketch_text.stroke-116"),sQuery(id+"F3.wireOp",EDGE,"E8.sketch_text.stroke-117"),sQuery(id+"F3.wireOp",EDGE,"E8.sketch_text.stroke-118")])]});
            var Q1;
            Q1=makeQuery(id+"F8.opPattern","COPY",BODY,{"derivedFrom":makeQuery(id+"F1.opRevolve","SWEPT_BODY",BODY,{"disambiguationData":[OSD([sQuery(id+"F0.wireOp",EDGE,"E2"),sQuery(id+"F0.wireOp",EDGE,"E5"),sQuery(id+"F0.wireOp",EDGE,"E6"),sQuery(id+"F0.wireOp",EDGE,"E7")])]}),"instanceName":"1"});
            booleanBodies(context, id + "F18", {"operationType" : BooleanOperationType.INTERSECTION, "tools" : qUnion([Q0, Q1]), "keepTools" : true});
        }
        {
            var Q0;
            Q0=makeQuery(id+"F4.opExtrude","SWEPT_BODY",BODY,{"disambiguationData":[OSD([sQuery(id+"F3.wireOp",EDGE,"E8.sketch_text.stroke-119"),sQuery(id+"F3.wireOp",EDGE,"E8.sketch_text.stroke-120"),sQuery(id+"F3.wireOp",EDGE,"E8.sketch_text.stroke-121"),sQuery(id+"F3.wireOp",EDGE,"E8.sketch_text.stroke-122"),sQuery(id+"F3.wireOp",EDGE,"E8.sketch_text.stroke-123"),sQuery(id+"F3.wireOp",EDGE,"E8.sketch_text.stroke-124"),sQuery(id+"F3.wireOp",EDGE,"E8.sketch_text.stroke-125"),sQuery(id+"F3.wireOp",EDGE,"E8.sketch_text.stroke-126"),sQuery(id+"F3.wireOp",EDGE,"E8.sketch_text.stroke-127"),sQuery(id+"F3.wireOp",EDGE,"E8.sketch_text.stroke-128"),sQuery(id+"F3.wireOp",EDGE,"E8.sketch_text.stroke-129"),sQuery(id+"F3.wireOp",EDGE,"E8.sketch_text.stroke-130"),sQuery(id+"F3.wireOp",EDGE,"E8.sketch_text.stroke-131"),sQuery(id+"F3.wireOp",EDGE,"E8.sketch_text.stroke-132"),sQuery(id+"F3.wireOp",EDGE,"E8.sketch_text.stroke-133"),sQuery(id+"F3.wireOp",EDGE,"E8.sketch_text.stroke-134"),sQuery(id+"F3.wireOp",EDGE,"E8.sketch_text.stroke-135"),sQuery(id+"F3.wireOp",EDGE,"E8.sketch_text.stroke-136"),sQuery(id+"F3.wireOp",EDGE,"E8.sketch_text.stroke-137"),sQuery(id+"F3.wireOp",EDGE,"E8.sketch_text.stroke-138"),sQuery(id+"F3.wireOp",EDGE,"E8.sketch_text.stroke-139"),sQuery(id+"F3.wireOp",EDGE,"E8.sketch_text.stroke-140"),sQuery(id+"F3.wireOp",EDGE,"E8.sketch_text.stroke-141"),sQuery(id+"F3.wireOp",EDGE,"E8.sketch_text.stroke-142")])]});
            var Q1;
            Q1=makeQuery(id+"F8.opPattern","COPY",BODY,{"derivedFrom":makeQuery(id+"F1.opRevolve","SWEPT_BODY",BODY,{"disambiguationData":[OSD([sQuery(id+"F0.wireOp",EDGE,"E2"),sQuery(id+"F0.wireOp",EDGE,"E5"),sQuery(id+"F0.wireOp",EDGE,"E6"),sQuery(id+"F0.wireOp",EDGE,"E7")])]}),"instanceName":"1"});
            booleanBodies(context, id + "F19", {"operationType" : BooleanOperationType.INTERSECTION, "tools" : qUnion([Q0, Q1]), "keepTools" : true});
        }
        {
            var Q0;
            Q0=makeQuery(id+"F4.opExtrude","SWEPT_BODY",BODY,{"disambiguationData":[OSD([sQuery(id+"F3.wireOp",EDGE,"E8.sketch_text.stroke-143"),sQuery(id+"F3.wireOp",EDGE,"E8.sketch_text.stroke-144"),sQuery(id+"F3.wireOp",EDGE,"E8.sketch_text.stroke-145"),sQuery(id+"F3.wireOp",EDGE,"E8.sketch_text.stroke-146")])]});
            var Q1;
            Q1=makeQuery(id+"F8.opPattern","COPY",BODY,{"derivedFrom":makeQuery(id+"F1.opRevolve","SWEPT_BODY",BODY,{"disambiguationData":[OSD([sQuery(id+"F0.wireOp",EDGE,"E2"),sQuery(id+"F0.wireOp",EDGE,"E5"),sQuery(id+"F0.wireOp",EDGE,"E6"),sQuery(id+"F0.wireOp",EDGE,"E7")])]}),"instanceName":"1"});
            booleanBodies(context, id + "F20", {"operationType" : BooleanOperationType.INTERSECTION, "tools" : qUnion([Q0, Q1]), "keepTools" : true});
        }
        {
            var Q0;
            Q0=makeQuery(id+"F4.opExtrude","SWEPT_BODY",BODY,{"disambiguationData":[OSD([sQuery(id+"F3.wireOp",EDGE,"E8.sketch_text.stroke-147"),sQuery(id+"F3.wireOp",EDGE,"E8.sketch_text.stroke-148"),sQuery(id+"F3.wireOp",EDGE,"E8.sketch_text.stroke-149"),sQuery(id+"F3.wireOp",EDGE,"E8.sketch_text.stroke-150"),sQuery(id+"F3.wireOp",EDGE,"E8.sketch_text.stroke-151"),sQuery(id+"F3.wireOp",EDGE,"E8.sketch_text.stroke-152"),sQuery(id+"F3.wireOp",EDGE,"E8.sketch_text.stroke-153")])]});
            var Q1;
            Q1=makeQuery(id+"F8.opPattern","COPY",BODY,{"derivedFrom":makeQuery(id+"F1.opRevolve","SWEPT_BODY",BODY,{"disambiguationData":[OSD([sQuery(id+"F0.wireOp",EDGE,"E2"),sQuery(id+"F0.wireOp",EDGE,"E5"),sQuery(id+"F0.wireOp",EDGE,"E6"),sQuery(id+"F0.wireOp",EDGE,"E7")])]}),"instanceName":"1"});
            booleanBodies(context, id + "F21", {"operationType" : BooleanOperationType.INTERSECTION, "tools" : qUnion([Q0, Q1]), "keepTools" : true});
        }
        {
            var Q0;
            Q0=makeQuery(id+"F9.opBoolean","INTERSECT",BODY,{"derivedFrom":[makeQuery(id+"F4.opExtrude","SWEPT_BODY",BODY,{"disambiguationData":[OSD([sQuery(id+"F3.wireOp",EDGE,"E8.sketch_text.stroke-0"),sQuery(id+"F3.wireOp",EDGE,"E8.sketch_text.stroke-1"),sQuery(id+"F3.wireOp",EDGE,"E8.sketch_text.stroke-2"),sQuery(id+"F3.wireOp",EDGE,"E8.sketch_text.stroke-3"),sQuery(id+"F3.wireOp",EDGE,"E8.sketch_text.stroke-4"),sQuery(id+"F3.wireOp",EDGE,"E8.sketch_text.stroke-5"),sQuery(id+"F3.wireOp",EDGE,"E8.sketch_text.stroke-6"),sQuery(id+"F3.wireOp",EDGE,"E8.sketch_text.stroke-7"),sQuery(id+"F3.wireOp",EDGE,"E8.sketch_text.stroke-8"),sQuery(id+"F3.wireOp",EDGE,"E8.sketch_text.stroke-9"),sQuery(id+"F3.wireOp",EDGE,"E8.sketch_text.stroke-10"),sQuery(id+"F3.wireOp",EDGE,"E8.sketch_text.stroke-11"),sQuery(id+"F3.wireOp",EDGE,"E8.sketch_text.stroke-12"),sQuery(id+"F3.wireOp",EDGE,"E8.sketch_text.stroke-13"),sQuery(id+"F3.wireOp",EDGE,"E8.sketch_text.stroke-14"),sQuery(id+"F3.wireOp",EDGE,"E8.sketch_text.stroke-15"),sQuery(id+"F3.wireOp",EDGE,"E8.sketch_text.stroke-16"),sQuery(id+"F3.wireOp",EDGE,"E8.sketch_text.stroke-17")])]}),makeQuery(id+"F8.opPattern","COPY",BODY,{"derivedFrom":makeQuery(id+"F1.opRevolve","SWEPT_BODY",BODY,{"disambiguationData":[OSD([sQuery(id+"F0.wireOp",EDGE,"E2"),sQuery(id+"F0.wireOp",EDGE,"E5"),sQuery(id+"F0.wireOp",EDGE,"E6"),sQuery(id+"F0.wireOp",EDGE,"E7")])]}),"instanceName":"1"})]});
            var Q1;
            Q1=makeQuery(id+"F10.opBoolean","INTERSECT",BODY,{"derivedFrom":[makeQuery(id+"F4.opExtrude","SWEPT_BODY",BODY,{"disambiguationData":[OSD([sQuery(id+"F3.wireOp",EDGE,"E8.sketch_text.stroke-18"),sQuery(id+"F3.wireOp",EDGE,"E8.sketch_text.stroke-19"),sQuery(id+"F3.wireOp",EDGE,"E8.sketch_text.stroke-20"),sQuery(id+"F3.wireOp",EDGE,"E8.sketch_text.stroke-21"),sQuery(id+"F3.wireOp",EDGE,"E8.sketch_text.stroke-22"),sQuery(id+"F3.wireOp",EDGE,"E8.sketch_text.stroke-23"),sQuery(id+"F3.wireOp",EDGE,"E8.sketch_text.stroke-24"),sQuery(id+"F3.wireOp",EDGE,"E8.sketch_text.stroke-25"),sQuery(id+"F3.wireOp",EDGE,"E8.sketch_text.stroke-26"),sQuery(id+"F3.wireOp",EDGE,"E8.sketch_text.stroke-27"),sQuery(id+"F3.wireOp",EDGE,"E8.sketch_text.stroke-28"),sQuery(id+"F3.wireOp",EDGE,"E8.sketch_text.stroke-29"),sQuery(id+"F3.wireOp",EDGE,"E8.sketch_text.stroke-30"),sQuery(id+"F3.wireOp",EDGE,"E8.sketch_text.stroke-31"),sQuery(id+"F3.wireOp",EDGE,"E8.sketch_text.stroke-32"),sQuery(id+"F3.wireOp",EDGE,"E8.sketch_text.stroke-33"),sQuery(id+"F3.wireOp",EDGE,"E8.sketch_text.stroke-34"),sQuery(id+"F3.wireOp",EDGE,"E8.sketch_text.stroke-35"),sQuery(id+"F3.wireOp",EDGE,"E8.sketch_text.stroke-36")])]}),makeQuery(id+"F8.opPattern","COPY",BODY,{"derivedFrom":makeQuery(id+"F1.opRevolve","SWEPT_BODY",BODY,{"disambiguationData":[OSD([sQuery(id+"F0.wireOp",EDGE,"E2"),sQuery(id+"F0.wireOp",EDGE,"E5"),sQuery(id+"F0.wireOp",EDGE,"E6"),sQuery(id+"F0.wireOp",EDGE,"E7")])]}),"instanceName":"1"})]});
            var Q2;
            Q2=makeQuery(id+"F11.opBoolean","INTERSECT",BODY,{"derivedFrom":[makeQuery(id+"F4.opExtrude","SWEPT_BODY",BODY,{"disambiguationData":[OSD([sQuery(id+"F3.wireOp",EDGE,"E8.sketch_text.stroke-37"),sQuery(id+"F3.wireOp",EDGE,"E8.sketch_text.stroke-38"),sQuery(id+"F3.wireOp",EDGE,"E8.sketch_text.stroke-39"),sQuery(id+"F3.wireOp",EDGE,"E8.sketch_text.stroke-40")])]}),makeQuery(id+"F8.opPattern","COPY",BODY,{"derivedFrom":makeQuery(id+"F1.opRevolve","SWEPT_BODY",BODY,{"disambiguationData":[OSD([sQuery(id+"F0.wireOp",EDGE,"E2"),sQuery(id+"F0.wireOp",EDGE,"E5"),sQuery(id+"F0.wireOp",EDGE,"E6"),sQuery(id+"F0.wireOp",EDGE,"E7")])]}),"instanceName":"1"})]});
            var Q3;
            Q3=makeQuery(id+"F12.opBoolean","INTERSECT",BODY,{"derivedFrom":[makeQuery(id+"F4.opExtrude","SWEPT_BODY",BODY,{"disambiguationData":[OSD([sQuery(id+"F3.wireOp",EDGE,"E8.sketch_text.stroke-41"),sQuery(id+"F3.wireOp",EDGE,"E8.sketch_text.stroke-42"),sQuery(id+"F3.wireOp",EDGE,"E8.sketch_text.stroke-43"),sQuery(id+"F3.wireOp",EDGE,"E8.sketch_text.stroke-44")])]}),makeQuery(id+"F8.opPattern","COPY",BODY,{"derivedFrom":makeQuery(id+"F1.opRevolve","SWEPT_BODY",BODY,{"disambiguationData":[OSD([sQuery(id+"F0.wireOp",EDGE,"E2"),sQuery(id+"F0.wireOp",EDGE,"E5"),sQuery(id+"F0.wireOp",EDGE,"E6"),sQuery(id+"F0.wireOp",EDGE,"E7")])]}),"instanceName":"1"})]});
            var Q4;
            Q4=makeQuery(id+"F13.opBoolean","INTERSECT",BODY,{"derivedFrom":[makeQuery(id+"F4.opExtrude","SWEPT_BODY",BODY,{"disambiguationData":[OSD([sQuery(id+"F3.wireOp",EDGE,"E8.sketch_text.stroke-45"),sQuery(id+"F3.wireOp",EDGE,"E8.sketch_text.stroke-46"),sQuery(id+"F3.wireOp",EDGE,"E8.sketch_text.stroke-47"),sQuery(id+"F3.wireOp",EDGE,"E8.sketch_text.stroke-48"),sQuery(id+"F3.wireOp",EDGE,"E8.sketch_text.stroke-49"),sQuery(id+"F3.wireOp",EDGE,"E8.sketch_text.stroke-50"),sQuery(id+"F3.wireOp",EDGE,"E8.sketch_text.stroke-51"),sQuery(id+"F3.wireOp",EDGE,"E8.sketch_text.stroke-52"),sQuery(id+"F3.wireOp",EDGE,"E8.sketch_text.stroke-53"),sQuery(id+"F3.wireOp",EDGE,"E8.sketch_text.stroke-54"),sQuery(id+"F3.wireOp",EDGE,"E8.sketch_text.stroke-55"),sQuery(id+"F3.wireOp",EDGE,"E8.sketch_text.stroke-56"),sQuery(id+"F3.wireOp",EDGE,"E8.sketch_text.stroke-57"),sQuery(id+"F3.wireOp",EDGE,"E8.sketch_text.stroke-58"),sQuery(id+"F3.wireOp",EDGE,"E8.sketch_text.stroke-59"),sQuery(id+"F3.wireOp",EDGE,"E8.sketch_text.stroke-60"),sQuery(id+"F3.wireOp",EDGE,"E8.sketch_text.stroke-61")])]}),makeQuery(id+"F8.opPattern","COPY",BODY,{"derivedFrom":makeQuery(id+"F1.opRevolve","SWEPT_BODY",BODY,{"disambiguationData":[OSD([sQuery(id+"F0.wireOp",EDGE,"E2"),sQuery(id+"F0.wireOp",EDGE,"E5"),sQuery(id+"F0.wireOp",EDGE,"E6"),sQuery(id+"F0.wireOp",EDGE,"E7")])]}),"instanceName":"1"})]});
            var Q5;
            Q5=makeQuery(id+"F14.opBoolean","INTERSECT",BODY,{"derivedFrom":[makeQuery(id+"F4.opExtrude","SWEPT_BODY",BODY,{"disambiguationData":[OSD([sQuery(id+"F3.wireOp",EDGE,"E8.sketch_text.stroke-62"),sQuery(id+"F3.wireOp",EDGE,"E8.sketch_text.stroke-63"),sQuery(id+"F3.wireOp",EDGE,"E8.sketch_text.stroke-64"),sQuery(id+"F3.wireOp",EDGE,"E8.sketch_text.stroke-65"),sQuery(id+"F3.wireOp",EDGE,"E8.sketch_text.stroke-66"),sQuery(id+"F3.wireOp",EDGE,"E8.sketch_text.stroke-67"),sQuery(id+"F3.wireOp",EDGE,"E8.sketch_text.stroke-68"),sQuery(id+"F3.wireOp",EDGE,"E8.sketch_text.stroke-69"),sQuery(id+"F3.wireOp",EDGE,"E8.sketch_text.stroke-70"),sQuery(id+"F3.wireOp",EDGE,"E8.sketch_text.stroke-71"),sQuery(id+"F3.wireOp",EDGE,"E8.sketch_text.stroke-72"),sQuery(id+"F3.wireOp",EDGE,"E8.sketch_text.stroke-73"),sQuery(id+"F3.wireOp",EDGE,"E8.sketch_text.stroke-74"),sQuery(id+"F3.wireOp",EDGE,"E8.sketch_text.stroke-75"),sQuery(id+"F3.wireOp",EDGE,"E8.sketch_text.stroke-76"),sQuery(id+"F3.wireOp",EDGE,"E8.sketch_text.stroke-77"),sQuery(id+"F3.wireOp",EDGE,"E8.sketch_text.stroke-78"),sQuery(id+"F3.wireOp",EDGE,"E8.sketch_text.stroke-79"),sQuery(id+"F3.wireOp",EDGE,"E8.sketch_text.stroke-80"),sQuery(id+"F3.wireOp",EDGE,"E8.sketch_text.stroke-81"),sQuery(id+"F3.wireOp",EDGE,"E8.sketch_text.stroke-82"),sQuery(id+"F3.wireOp",EDGE,"E8.sketch_text.stroke-83"),sQuery(id+"F3.wireOp",EDGE,"E8.sketch_text.stroke-84")])]}),makeQuery(id+"F8.opPattern","COPY",BODY,{"derivedFrom":makeQuery(id+"F1.opRevolve","SWEPT_BODY",BODY,{"disambiguationData":[OSD([sQuery(id+"F0.wireOp",EDGE,"E2"),sQuery(id+"F0.wireOp",EDGE,"E5"),sQuery(id+"F0.wireOp",EDGE,"E6"),sQuery(id+"F0.wireOp",EDGE,"E7")])]}),"instanceName":"1"})]});
            var Q6;
            Q6=makeQuery(id+"F15.opBoolean","INTERSECT",BODY,{"derivedFrom":[makeQuery(id+"F4.opExtrude","SWEPT_BODY",BODY,{"disambiguationData":[OSD([sQuery(id+"F3.wireOp",EDGE,"E8.sketch_text.stroke-85"),sQuery(id+"F3.wireOp",EDGE,"E8.sketch_text.stroke-86"),sQuery(id+"F3.wireOp",EDGE,"E8.sketch_text.stroke-87"),sQuery(id+"F3.wireOp",EDGE,"E8.sketch_text.stroke-88"),sQuery(id+"F3.wireOp",EDGE,"E8.sketch_text.stroke-89"),sQuery(id+"F3.wireOp",EDGE,"E8.sketch_text.stroke-90"),sQuery(id+"F3.wireOp",EDGE,"E8.sketch_text.stroke-91"),sQuery(id+"F3.wireOp",EDGE,"E8.sketch_text.stroke-92"),sQuery(id+"F3.wireOp",EDGE,"E8.sketch_text.stroke-93"),sQuery(id+"F3.wireOp",EDGE,"E8.sketch_text.stroke-94"),sQuery(id+"F3.wireOp",EDGE,"E8.sketch_text.stroke-95"),sQuery(id+"F3.wireOp",EDGE,"E8.sketch_text.stroke-96"),sQuery(id+"F3.wireOp",EDGE,"E8.sketch_text.stroke-97"),sQuery(id+"F3.wireOp",EDGE,"E8.sketch_text.stroke-98"),sQuery(id+"F3.wireOp",EDGE,"E8.sketch_text.stroke-99"),sQuery(id+"F3.wireOp",EDGE,"E8.sketch_text.stroke-100"),sQuery(id+"F3.wireOp",EDGE,"E8.sketch_text.stroke-101")])]}),makeQuery(id+"F8.opPattern","COPY",BODY,{"derivedFrom":makeQuery(id+"F1.opRevolve","SWEPT_BODY",BODY,{"disambiguationData":[OSD([sQuery(id+"F0.wireOp",EDGE,"E2"),sQuery(id+"F0.wireOp",EDGE,"E5"),sQuery(id+"F0.wireOp",EDGE,"E6"),sQuery(id+"F0.wireOp",EDGE,"E7")])]}),"instanceName":"1"})]});
            var Q7;
            Q7=makeQuery(id+"F16.opBoolean","INTERSECT",BODY,{"derivedFrom":[makeQuery(id+"F4.opExtrude","SWEPT_BODY",BODY,{"disambiguationData":[OSD([sQuery(id+"F3.wireOp",EDGE,"E8.sketch_text.stroke-102"),sQuery(id+"F3.wireOp",EDGE,"E8.sketch_text.stroke-103"),sQuery(id+"F3.wireOp",EDGE,"E8.sketch_text.stroke-104"),sQuery(id+"F3.wireOp",EDGE,"E8.sketch_text.stroke-105"),sQuery(id+"F3.wireOp",EDGE,"E8.sketch_text.stroke-106"),sQuery(id+"F3.wireOp",EDGE,"E8.sketch_text.stroke-107"),sQuery(id+"F3.wireOp",EDGE,"E8.sketch_text.stroke-108"),sQuery(id+"F3.wireOp",EDGE,"E8.sketch_text.stroke-109"),sQuery(id+"F3.wireOp",EDGE,"E8.sketch_text.stroke-110"),sQuery(id+"F3.wireOp",EDGE,"E8.sketch_text.stroke-111"),sQuery(id+"F3.wireOp",EDGE,"E8.sketch_text.stroke-112"),sQuery(id+"F3.wireOp",EDGE,"E8.sketch_text.stroke-113"),sQuery(id+"F3.wireOp",EDGE,"E8.sketch_text.stroke-114")])]}),makeQuery(id+"F8.opPattern","COPY",BODY,{"derivedFrom":makeQuery(id+"F1.opRevolve","SWEPT_BODY",BODY,{"disambiguationData":[OSD([sQuery(id+"F0.wireOp",EDGE,"E2"),sQuery(id+"F0.wireOp",EDGE,"E5"),sQuery(id+"F0.wireOp",EDGE,"E6"),sQuery(id+"F0.wireOp",EDGE,"E7")])]}),"instanceName":"1"})]});
            var Q8;
            Q8=makeQuery(id+"F17.opBoolean","INTERSECT",BODY,{"derivedFrom":[makeQuery(id+"F4.opExtrude","SWEPT_BODY",BODY,{"disambiguationData":[OSD([sQuery(id+"F3.wireOp",EDGE,"E8.sketch_text.stroke-115"),sQuery(id+"F3.wireOp",EDGE,"E8.sketch_text.stroke-116"),sQuery(id+"F3.wireOp",EDGE,"E8.sketch_text.stroke-117"),sQuery(id+"F3.wireOp",EDGE,"E8.sketch_text.stroke-118")])]}),makeQuery(id+"F8.opPattern","COPY",BODY,{"derivedFrom":makeQuery(id+"F1.opRevolve","SWEPT_BODY",BODY,{"disambiguationData":[OSD([sQuery(id+"F0.wireOp",EDGE,"E2"),sQuery(id+"F0.wireOp",EDGE,"E5"),sQuery(id+"F0.wireOp",EDGE,"E6"),sQuery(id+"F0.wireOp",EDGE,"E7")])]}),"instanceName":"1"})]});
            var Q9;
            Q9=makeQuery(id+"F18.opBoolean","INTERSECT",BODY,{"derivedFrom":[makeQuery(id+"F4.opExtrude","SWEPT_BODY",BODY,{"disambiguationData":[OSD([sQuery(id+"F3.wireOp",EDGE,"E8.sketch_text.stroke-115"),sQuery(id+"F3.wireOp",EDGE,"E8.sketch_text.stroke-116"),sQuery(id+"F3.wireOp",EDGE,"E8.sketch_text.stroke-117"),sQuery(id+"F3.wireOp",EDGE,"E8.sketch_text.stroke-118")])]}),makeQuery(id+"F8.opPattern","COPY",BODY,{"derivedFrom":makeQuery(id+"F1.opRevolve","SWEPT_BODY",BODY,{"disambiguationData":[OSD([sQuery(id+"F0.wireOp",EDGE,"E2"),sQuery(id+"F0.wireOp",EDGE,"E5"),sQuery(id+"F0.wireOp",EDGE,"E6"),sQuery(id+"F0.wireOp",EDGE,"E7")])]}),"instanceName":"1"})]});
            var Q10;
            Q10=makeQuery(id+"F19.opBoolean","INTERSECT",BODY,{"derivedFrom":[makeQuery(id+"F4.opExtrude","SWEPT_BODY",BODY,{"disambiguationData":[OSD([sQuery(id+"F3.wireOp",EDGE,"E8.sketch_text.stroke-119"),sQuery(id+"F3.wireOp",EDGE,"E8.sketch_text.stroke-120"),sQuery(id+"F3.wireOp",EDGE,"E8.sketch_text.stroke-121"),sQuery(id+"F3.wireOp",EDGE,"E8.sketch_text.stroke-122"),sQuery(id+"F3.wireOp",EDGE,"E8.sketch_text.stroke-123"),sQuery(id+"F3.wireOp",EDGE,"E8.sketch_text.stroke-124"),sQuery(id+"F3.wireOp",EDGE,"E8.sketch_text.stroke-125"),sQuery(id+"F3.wireOp",EDGE,"E8.sketch_text.stroke-126"),sQuery(id+"F3.wireOp",EDGE,"E8.sketch_text.stroke-127"),sQuery(id+"F3.wireOp",EDGE,"E8.sketch_text.stroke-128"),sQuery(id+"F3.wireOp",EDGE,"E8.sketch_text.stroke-129"),sQuery(id+"F3.wireOp",EDGE,"E8.sketch_text.stroke-130"),sQuery(id+"F3.wireOp",EDGE,"E8.sketch_text.stroke-131"),sQuery(id+"F3.wireOp",EDGE,"E8.sketch_text.stroke-132"),sQuery(id+"F3.wireOp",EDGE,"E8.sketch_text.stroke-133"),sQuery(id+"F3.wireOp",EDGE,"E8.sketch_text.stroke-134"),sQuery(id+"F3.wireOp",EDGE,"E8.sketch_text.stroke-135"),sQuery(id+"F3.wireOp",EDGE,"E8.sketch_text.stroke-136"),sQuery(id+"F3.wireOp",EDGE,"E8.sketch_text.stroke-137"),sQuery(id+"F3.wireOp",EDGE,"E8.sketch_text.stroke-138"),sQuery(id+"F3.wireOp",EDGE,"E8.sketch_text.stroke-139"),sQuery(id+"F3.wireOp",EDGE,"E8.sketch_text.stroke-140"),sQuery(id+"F3.wireOp",EDGE,"E8.sketch_text.stroke-141"),sQuery(id+"F3.wireOp",EDGE,"E8.sketch_text.stroke-142")])]}),makeQuery(id+"F8.opPattern","COPY",BODY,{"derivedFrom":makeQuery(id+"F1.opRevolve","SWEPT_BODY",BODY,{"disambiguationData":[OSD([sQuery(id+"F0.wireOp",EDGE,"E2"),sQuery(id+"F0.wireOp",EDGE,"E5"),sQuery(id+"F0.wireOp",EDGE,"E6"),sQuery(id+"F0.wireOp",EDGE,"E7")])]}),"instanceName":"1"})]});
            var Q11;
            Q11=makeQuery(id+"F20.opBoolean","INTERSECT",BODY,{"derivedFrom":[makeQuery(id+"F4.opExtrude","SWEPT_BODY",BODY,{"disambiguationData":[OSD([sQuery(id+"F3.wireOp",EDGE,"E8.sketch_text.stroke-143"),sQuery(id+"F3.wireOp",EDGE,"E8.sketch_text.stroke-144"),sQuery(id+"F3.wireOp",EDGE,"E8.sketch_text.stroke-145"),sQuery(id+"F3.wireOp",EDGE,"E8.sketch_text.stroke-146")])]}),makeQuery(id+"F8.opPattern","COPY",BODY,{"derivedFrom":makeQuery(id+"F1.opRevolve","SWEPT_BODY",BODY,{"disambiguationData":[OSD([sQuery(id+"F0.wireOp",EDGE,"E2"),sQuery(id+"F0.wireOp",EDGE,"E5"),sQuery(id+"F0.wireOp",EDGE,"E6"),sQuery(id+"F0.wireOp",EDGE,"E7")])]}),"instanceName":"1"})]});
            var Q12;
            Q12=makeQuery(id+"F21.opBoolean","INTERSECT",BODY,{"derivedFrom":[makeQuery(id+"F4.opExtrude","SWEPT_BODY",BODY,{"disambiguationData":[OSD([sQuery(id+"F3.wireOp",EDGE,"E8.sketch_text.stroke-147"),sQuery(id+"F3.wireOp",EDGE,"E8.sketch_text.stroke-148"),sQuery(id+"F3.wireOp",EDGE,"E8.sketch_text.stroke-149"),sQuery(id+"F3.wireOp",EDGE,"E8.sketch_text.stroke-150"),sQuery(id+"F3.wireOp",EDGE,"E8.sketch_text.stroke-151"),sQuery(id+"F3.wireOp",EDGE,"E8.sketch_text.stroke-152"),sQuery(id+"F3.wireOp",EDGE,"E8.sketch_text.stroke-153")])]}),makeQuery(id+"F8.opPattern","COPY",BODY,{"derivedFrom":makeQuery(id+"F1.opRevolve","SWEPT_BODY",BODY,{"disambiguationData":[OSD([sQuery(id+"F0.wireOp",EDGE,"E2"),sQuery(id+"F0.wireOp",EDGE,"E5"),sQuery(id+"F0.wireOp",EDGE,"E6"),sQuery(id+"F0.wireOp",EDGE,"E7")])]}),"instanceName":"1"})]});
            transform(context, id + "F22", {"entities" : qUnion([Q0, Q1, Q2, Q3, Q4, Q5, Q6, Q7, Q8, Q9, Q10, Q11, Q12]), "transformType" : TransformType.TRANSLATION_3D, "dx" : 0 * mm, "dy" : 0 * mm, "dz" : 1 * mm, "makeCopy" : false});
        }
        {
            var Q0;
            Q0=makeQuery(id+"F4.opExtrude","SWEPT_BODY",BODY,{"disambiguationData":[OSD([sQuery(id+"F3.wireOp",EDGE,"E8.sketch_text.stroke-0"),sQuery(id+"F3.wireOp",EDGE,"E8.sketch_text.stroke-1"),sQuery(id+"F3.wireOp",EDGE,"E8.sketch_text.stroke-2"),sQuery(id+"F3.wireOp",EDGE,"E8.sketch_text.stroke-3"),sQuery(id+"F3.wireOp",EDGE,"E8.sketch_text.stroke-4"),sQuery(id+"F3.wireOp",EDGE,"E8.sketch_text.stroke-5"),sQuery(id+"F3.wireOp",EDGE,"E8.sketch_text.stroke-6"),sQuery(id+"F3.wireOp",EDGE,"E8.sketch_text.stroke-7"),sQuery(id+"F3.wireOp",EDGE,"E8.sketch_text.stroke-8"),sQuery(id+"F3.wireOp",EDGE,"E8.sketch_text.stroke-9"),sQuery(id+"F3.wireOp",EDGE,"E8.sketch_text.stroke-10"),sQuery(id+"F3.wireOp",EDGE,"E8.sketch_text.stroke-11"),sQuery(id+"F3.wireOp",EDGE,"E8.sketch_text.stroke-12"),sQuery(id+"F3.wireOp",EDGE,"E8.sketch_text.stroke-13"),sQuery(id+"F3.wireOp",EDGE,"E8.sketch_text.stroke-14"),sQuery(id+"F3.wireOp",EDGE,"E8.sketch_text.stroke-15"),sQuery(id+"F3.wireOp",EDGE,"E8.sketch_text.stroke-16"),sQuery(id+"F3.wireOp",EDGE,"E8.sketch_text.stroke-17")])]});
            var Q1;
            Q1=makeQuery(id+"F4.opExtrude","SWEPT_BODY",BODY,{"disambiguationData":[OSD([sQuery(id+"F3.wireOp",EDGE,"E8.sketch_text.stroke-18"),sQuery(id+"F3.wireOp",EDGE,"E8.sketch_text.stroke-19"),sQuery(id+"F3.wireOp",EDGE,"E8.sketch_text.stroke-20"),sQuery(id+"F3.wireOp",EDGE,"E8.sketch_text.stroke-21"),sQuery(id+"F3.wireOp",EDGE,"E8.sketch_text.stroke-22"),sQuery(id+"F3.wireOp",EDGE,"E8.sketch_text.stroke-23"),sQuery(id+"F3.wireOp",EDGE,"E8.sketch_text.stroke-24"),sQuery(id+"F3.wireOp",EDGE,"E8.sketch_text.stroke-25"),sQuery(id+"F3.wireOp",EDGE,"E8.sketch_text.stroke-26"),sQuery(id+"F3.wireOp",EDGE,"E8.sketch_text.stroke-27"),sQuery(id+"F3.wireOp",EDGE,"E8.sketch_text.stroke-28"),sQuery(id+"F3.wireOp",EDGE,"E8.sketch_text.stroke-29"),sQuery(id+"F3.wireOp",EDGE,"E8.sketch_text.stroke-30"),sQuery(id+"F3.wireOp",EDGE,"E8.sketch_text.stroke-31"),sQuery(id+"F3.wireOp",EDGE,"E8.sketch_text.stroke-32"),sQuery(id+"F3.wireOp",EDGE,"E8.sketch_text.stroke-33"),sQuery(id+"F3.wireOp",EDGE,"E8.sketch_text.stroke-34"),sQuery(id+"F3.wireOp",EDGE,"E8.sketch_text.stroke-35"),sQuery(id+"F3.wireOp",EDGE,"E8.sketch_text.stroke-36")])]});
            var Q2;
            Q2=makeQuery(id+"F4.opExtrude","SWEPT_BODY",BODY,{"disambiguationData":[OSD([sQuery(id+"F3.wireOp",EDGE,"E8.sketch_text.stroke-37"),sQuery(id+"F3.wireOp",EDGE,"E8.sketch_text.stroke-38"),sQuery(id+"F3.wireOp",EDGE,"E8.sketch_text.stroke-39"),sQuery(id+"F3.wireOp",EDGE,"E8.sketch_text.stroke-40")])]});
            var Q3;
            Q3=makeQuery(id+"F4.opExtrude","SWEPT_BODY",BODY,{"disambiguationData":[OSD([sQuery(id+"F3.wireOp",EDGE,"E8.sketch_text.stroke-41"),sQuery(id+"F3.wireOp",EDGE,"E8.sketch_text.stroke-42"),sQuery(id+"F3.wireOp",EDGE,"E8.sketch_text.stroke-43"),sQuery(id+"F3.wireOp",EDGE,"E8.sketch_text.stroke-44")])]});
            var Q4;
            Q4=makeQuery(id+"F4.opExtrude","SWEPT_BODY",BODY,{"disambiguationData":[OSD([sQuery(id+"F3.wireOp",EDGE,"E8.sketch_text.stroke-45"),sQuery(id+"F3.wireOp",EDGE,"E8.sketch_text.stroke-46"),sQuery(id+"F3.wireOp",EDGE,"E8.sketch_text.stroke-47"),sQuery(id+"F3.wireOp",EDGE,"E8.sketch_text.stroke-48"),sQuery(id+"F3.wireOp",EDGE,"E8.sketch_text.stroke-49"),sQuery(id+"F3.wireOp",EDGE,"E8.sketch_text.stroke-50"),sQuery(id+"F3.wireOp",EDGE,"E8.sketch_text.stroke-51"),sQuery(id+"F3.wireOp",EDGE,"E8.sketch_text.stroke-52"),sQuery(id+"F3.wireOp",EDGE,"E8.sketch_text.stroke-53"),sQuery(id+"F3.wireOp",EDGE,"E8.sketch_text.stroke-54"),sQuery(id+"F3.wireOp",EDGE,"E8.sketch_text.stroke-55"),sQuery(id+"F3.wireOp",EDGE,"E8.sketch_text.stroke-56"),sQuery(id+"F3.wireOp",EDGE,"E8.sketch_text.stroke-57"),sQuery(id+"F3.wireOp",EDGE,"E8.sketch_text.stroke-58"),sQuery(id+"F3.wireOp",EDGE,"E8.sketch_text.stroke-59"),sQuery(id+"F3.wireOp",EDGE,"E8.sketch_text.stroke-60"),sQuery(id+"F3.wireOp",EDGE,"E8.sketch_text.stroke-61")])]});
            var Q5;
            Q5=makeQuery(id+"F4.opExtrude","SWEPT_BODY",BODY,{"disambiguationData":[OSD([sQuery(id+"F3.wireOp",EDGE,"E8.sketch_text.stroke-62"),sQuery(id+"F3.wireOp",EDGE,"E8.sketch_text.stroke-63"),sQuery(id+"F3.wireOp",EDGE,"E8.sketch_text.stroke-64"),sQuery(id+"F3.wireOp",EDGE,"E8.sketch_text.stroke-65"),sQuery(id+"F3.wireOp",EDGE,"E8.sketch_text.stroke-66"),sQuery(id+"F3.wireOp",EDGE,"E8.sketch_text.stroke-67"),sQuery(id+"F3.wireOp",EDGE,"E8.sketch_text.stroke-68"),sQuery(id+"F3.wireOp",EDGE,"E8.sketch_text.stroke-69"),sQuery(id+"F3.wireOp",EDGE,"E8.sketch_text.stroke-70"),sQuery(id+"F3.wireOp",EDGE,"E8.sketch_text.stroke-71"),sQuery(id+"F3.wireOp",EDGE,"E8.sketch_text.stroke-72"),sQuery(id+"F3.wireOp",EDGE,"E8.sketch_text.stroke-73"),sQuery(id+"F3.wireOp",EDGE,"E8.sketch_text.stroke-74"),sQuery(id+"F3.wireOp",EDGE,"E8.sketch_text.stroke-75"),sQuery(id+"F3.wireOp",EDGE,"E8.sketch_text.stroke-76"),sQuery(id+"F3.wireOp",EDGE,"E8.sketch_text.stroke-77"),sQuery(id+"F3.wireOp",EDGE,"E8.sketch_text.stroke-78"),sQuery(id+"F3.wireOp",EDGE,"E8.sketch_text.stroke-79"),sQuery(id+"F3.wireOp",EDGE,"E8.sketch_text.stroke-80"),sQuery(id+"F3.wireOp",EDGE,"E8.sketch_text.stroke-81"),sQuery(id+"F3.wireOp",EDGE,"E8.sketch_text.stroke-82"),sQuery(id+"F3.wireOp",EDGE,"E8.sketch_text.stroke-83"),sQuery(id+"F3.wireOp",EDGE,"E8.sketch_text.stroke-84")])]});
            var Q6;
            Q6=makeQuery(id+"F4.opExtrude","SWEPT_BODY",BODY,{"disambiguationData":[OSD([sQuery(id+"F3.wireOp",EDGE,"E8.sketch_text.stroke-85"),sQuery(id+"F3.wireOp",EDGE,"E8.sketch_text.stroke-86"),sQuery(id+"F3.wireOp",EDGE,"E8.sketch_text.stroke-87"),sQuery(id+"F3.wireOp",EDGE,"E8.sketch_text.stroke-88"),sQuery(id+"F3.wireOp",EDGE,"E8.sketch_text.stroke-89"),sQuery(id+"F3.wireOp",EDGE,"E8.sketch_text.stroke-90"),sQuery(id+"F3.wireOp",EDGE,"E8.sketch_text.stroke-91"),sQuery(id+"F3.wireOp",EDGE,"E8.sketch_text.stroke-92"),sQuery(id+"F3.wireOp",EDGE,"E8.sketch_text.stroke-93"),sQuery(id+"F3.wireOp",EDGE,"E8.sketch_text.stroke-94"),sQuery(id+"F3.wireOp",EDGE,"E8.sketch_text.stroke-95"),sQuery(id+"F3.wireOp",EDGE,"E8.sketch_text.stroke-96"),sQuery(id+"F3.wireOp",EDGE,"E8.sketch_text.stroke-97"),sQuery(id+"F3.wireOp",EDGE,"E8.sketch_text.stroke-98"),sQuery(id+"F3.wireOp",EDGE,"E8.sketch_text.stroke-99"),sQuery(id+"F3.wireOp",EDGE,"E8.sketch_text.stroke-100"),sQuery(id+"F3.wireOp",EDGE,"E8.sketch_text.stroke-101")])]});
            var Q7;
            Q7=makeQuery(id+"F4.opExtrude","SWEPT_BODY",BODY,{"disambiguationData":[OSD([sQuery(id+"F3.wireOp",EDGE,"E8.sketch_text.stroke-102"),sQuery(id+"F3.wireOp",EDGE,"E8.sketch_text.stroke-103"),sQuery(id+"F3.wireOp",EDGE,"E8.sketch_text.stroke-104"),sQuery(id+"F3.wireOp",EDGE,"E8.sketch_text.stroke-105"),sQuery(id+"F3.wireOp",EDGE,"E8.sketch_text.stroke-106"),sQuery(id+"F3.wireOp",EDGE,"E8.sketch_text.stroke-107"),sQuery(id+"F3.wireOp",EDGE,"E8.sketch_text.stroke-108"),sQuery(id+"F3.wireOp",EDGE,"E8.sketch_text.stroke-109"),sQuery(id+"F3.wireOp",EDGE,"E8.sketch_text.stroke-110"),sQuery(id+"F3.wireOp",EDGE,"E8.sketch_text.stroke-111"),sQuery(id+"F3.wireOp",EDGE,"E8.sketch_text.stroke-112"),sQuery(id+"F3.wireOp",EDGE,"E8.sketch_text.stroke-113"),sQuery(id+"F3.wireOp",EDGE,"E8.sketch_text.stroke-114")])]});
            var Q8;
            Q8=makeQuery(id+"F4.opExtrude","SWEPT_BODY",BODY,{"disambiguationData":[OSD([sQuery(id+"F3.wireOp",EDGE,"E8.sketch_text.stroke-115"),sQuery(id+"F3.wireOp",EDGE,"E8.sketch_text.stroke-116"),sQuery(id+"F3.wireOp",EDGE,"E8.sketch_text.stroke-117"),sQuery(id+"F3.wireOp",EDGE,"E8.sketch_text.stroke-118")])]});
            var Q9;
            Q9=makeQuery(id+"F4.opExtrude","SWEPT_BODY",BODY,{"disambiguationData":[OSD([sQuery(id+"F3.wireOp",EDGE,"E8.sketch_text.stroke-119"),sQuery(id+"F3.wireOp",EDGE,"E8.sketch_text.stroke-120"),sQuery(id+"F3.wireOp",EDGE,"E8.sketch_text.stroke-121"),sQuery(id+"F3.wireOp",EDGE,"E8.sketch_text.stroke-122"),sQuery(id+"F3.wireOp",EDGE,"E8.sketch_text.stroke-123"),sQuery(id+"F3.wireOp",EDGE,"E8.sketch_text.stroke-124"),sQuery(id+"F3.wireOp",EDGE,"E8.sketch_text.stroke-125"),sQuery(id+"F3.wireOp",EDGE,"E8.sketch_text.stroke-126"),sQuery(id+"F3.wireOp",EDGE,"E8.sketch_text.stroke-127"),sQuery(id+"F3.wireOp",EDGE,"E8.sketch_text.stroke-128"),sQuery(id+"F3.wireOp",EDGE,"E8.sketch_text.stroke-129"),sQuery(id+"F3.wireOp",EDGE,"E8.sketch_text.stroke-130"),sQuery(id+"F3.wireOp",EDGE,"E8.sketch_text.stroke-131"),sQuery(id+"F3.wireOp",EDGE,"E8.sketch_text.stroke-132"),sQuery(id+"F3.wireOp",EDGE,"E8.sketch_text.stroke-133"),sQuery(id+"F3.wireOp",EDGE,"E8.sketch_text.stroke-134"),sQuery(id+"F3.wireOp",EDGE,"E8.sketch_text.stroke-135"),sQuery(id+"F3.wireOp",EDGE,"E8.sketch_text.stroke-136"),sQuery(id+"F3.wireOp",EDGE,"E8.sketch_text.stroke-137"),sQuery(id+"F3.wireOp",EDGE,"E8.sketch_text.stroke-138"),sQuery(id+"F3.wireOp",EDGE,"E8.sketch_text.stroke-139"),sQuery(id+"F3.wireOp",EDGE,"E8.sketch_text.stroke-140"),sQuery(id+"F3.wireOp",EDGE,"E8.sketch_text.stroke-141"),sQuery(id+"F3.wireOp",EDGE,"E8.sketch_text.stroke-142")])]});
            var Q10;
            Q10=makeQuery(id+"F4.opExtrude","SWEPT_BODY",BODY,{"disambiguationData":[OSD([sQuery(id+"F3.wireOp",EDGE,"E8.sketch_text.stroke-143"),sQuery(id+"F3.wireOp",EDGE,"E8.sketch_text.stroke-144"),sQuery(id+"F3.wireOp",EDGE,"E8.sketch_text.stroke-145"),sQuery(id+"F3.wireOp",EDGE,"E8.sketch_text.stroke-146")])]});
            var Q11;
            Q11=makeQuery(id+"F4.opExtrude","SWEPT_BODY",BODY,{"disambiguationData":[OSD([sQuery(id+"F3.wireOp",EDGE,"E8.sketch_text.stroke-147"),sQuery(id+"F3.wireOp",EDGE,"E8.sketch_text.stroke-148"),sQuery(id+"F3.wireOp",EDGE,"E8.sketch_text.stroke-149"),sQuery(id+"F3.wireOp",EDGE,"E8.sketch_text.stroke-150"),sQuery(id+"F3.wireOp",EDGE,"E8.sketch_text.stroke-151"),sQuery(id+"F3.wireOp",EDGE,"E8.sketch_text.stroke-152"),sQuery(id+"F3.wireOp",EDGE,"E8.sketch_text.stroke-153")])]});
            var Q12;
            Q12=makeQuery(id+"F8.opPattern","COPY",BODY,{"derivedFrom":makeQuery(id+"F1.opRevolve","SWEPT_BODY",BODY,{"disambiguationData":[OSD([sQuery(id+"F0.wireOp",EDGE,"E2"),sQuery(id+"F0.wireOp",EDGE,"E5"),sQuery(id+"F0.wireOp",EDGE,"E6"),sQuery(id+"F0.wireOp",EDGE,"E7")])]}),"instanceName":"1"});
            deleteBodies(context, id + "F23", {"entities" : qUnion([Q0, Q1, Q2, Q3, Q4, Q5, Q6, Q7, Q8, Q9, Q10, Q11, Q12])});
        }
    });
